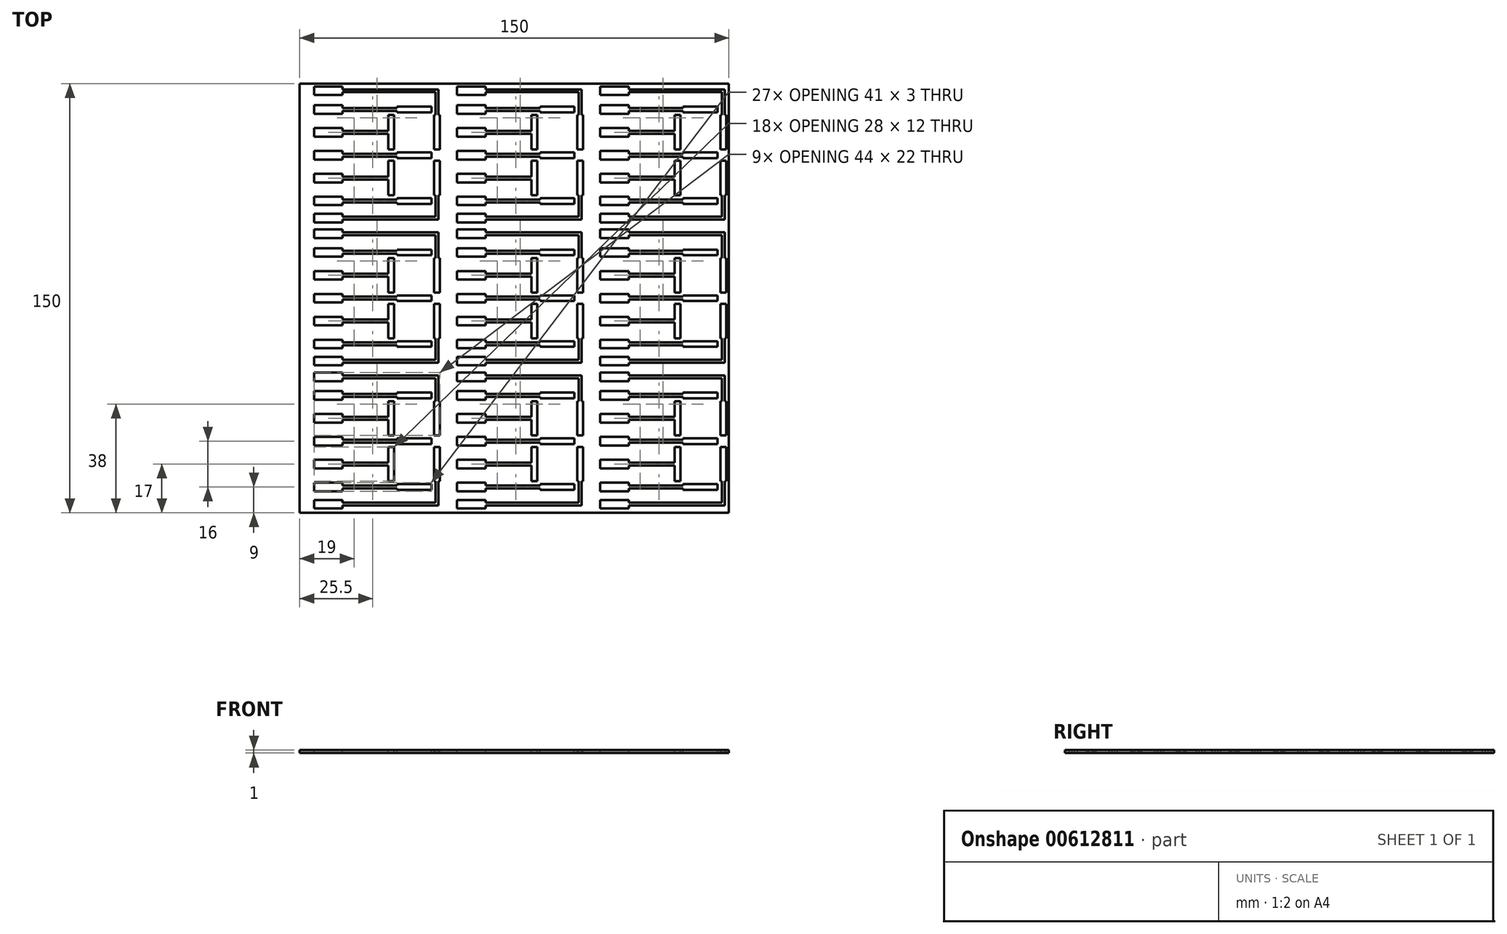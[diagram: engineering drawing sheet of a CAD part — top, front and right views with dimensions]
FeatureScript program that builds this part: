
annotation { "Feature Type Name" : "Feature", "Feature Type Description" : "" }
export const myFeature = defineFeature(function(context is Context, id is Id, definition is map)
    precondition{}
    {
        {
            var Q0;
            Q0=qCreatedBy(makeId("Top.planeOp"),FACE);
            var sketch = newSketch(context, id + "F0", { "sketchPlane" : qUnion([Q0])});
            skLineSegment(sketch, "E0.bottom", {"start": v(0, 0) * mm, "end": v(150, 0) * mm});
            skLineSegment(sketch, "E0.top", {"start": v(0, 150) * mm, "end": v(150, 150) * mm});
            skLineSegment(sketch, "E0.left", {"start": v(0, 0) * mm, "end": v(0, 150) * mm});
            skLineSegment(sketch, "E0.right", {"start": v(150, 0) * mm, "end": v(150, 150) * mm});
            skSolve(sketch);
        }
        {
            var Q0;
            Q0 = qSketchRegion(id + "F0", true);
            extrude(context, id + "F1", {"entities" : qUnion([Q0]), "depth" : 1 * mm, "offsetDistance" : 25 * mm});
        }
        {
            var Q0;
            Q0=makeQuery(id+"F1.opExtrude","CAP_FACE",FACE,{"disambiguationData":[OSD([sQuery(id+"F0.wireOp",EDGE,"E0.bottom"),sQuery(id+"F0.wireOp",EDGE,"E0.top"),sQuery(id+"F0.wireOp",EDGE,"E0.left"),sQuery(id+"F0.wireOp",EDGE,"E0.right")])],"isStart":false});
            var sketch = newSketch(context, id + "F2", { "sketchPlane" : qUnion([Q0])});
            skLineSegment(sketch, "E1", {"start": v(50, 150) * mm, "end": v(50, 0) * mm, "construction": true});
            skLineSegment(sketch, "E2", {"start": v(100, 150) * mm, "end": v(100, 0) * mm, "construction": true});
            skLineSegment(sketch, "E3", {"start": v(0, 100) * mm, "end": v(150, 100) * mm, "construction": true});
            skLineSegment(sketch, "E4", {"start": v(0, 50) * mm, "end": v(150, 50) * mm, "construction": true});
            skSolve(sketch);
        }
        {
            var Q0;
            Q0=makeQuery(id+"F2.imprint","IMPRINT",FACE,{"disambiguationData":[TD([[makeQuery(id+"F2.imprint","IMPRINT",EDGE,{"derivedFrom":makeQuery(id+"F1.opExtrude","CAP_EDGE",EDGE,{"disambiguationData":[OSD([sQuery(id+"F0.wireOp",EDGE,"E0.bottom")])],"isStart":false})}),1.0]])]});
            var sketch = newSketch(context, id + "F3", { "sketchPlane" : qUnion([Q0])});
            skLineSegment(sketch, "E5.bottom", {"start": v(34, 142) * mm, "end": v(46, 142) * mm});
            skLineSegment(sketch, "E5.top", {"start": v(34, 140) * mm, "end": v(46, 140) * mm});
            skLineSegment(sketch, "E5.left", {"start": v(34, 142) * mm, "end": v(34, 141.5) * mm});
            skLineSegment(sketch, "E5.right", {"start": v(46, 142) * mm, "end": v(46, 140) * mm});
            skLineSegment(sketch, "E6.bottom", {"start": v(47, 139) * mm, "end": v(49, 139) * mm});
            skLineSegment(sketch, "E6.top", {"start": v(47, 127) * mm, "end": v(49, 127) * mm});
            skLineSegment(sketch, "E6.left", {"start": v(47, 139) * mm, "end": v(47, 127) * mm});
            skLineSegment(sketch, "E6.right", {"start": v(49, 139) * mm, "end": v(49, 127) * mm});
            skLineSegment(sketch, "E7.bottom", {"start": v(46, 126) * mm, "end": v(34, 126) * mm});
            skLineSegment(sketch, "E7.top", {"start": v(46, 124) * mm, "end": v(34, 124) * mm});
            skLineSegment(sketch, "E7.left", {"start": v(46, 126) * mm, "end": v(46, 124) * mm});
            skLineSegment(sketch, "E7.right", {"start": v(34, 126) * mm, "end": v(34, 125.5) * mm});
            skLineSegment(sketch, "E8.bottom", {"start": v(47, 123) * mm, "end": v(49, 123) * mm});
            skLineSegment(sketch, "E8.top", {"start": v(47, 111) * mm, "end": v(47.5, 111) * mm});
            skLineSegment(sketch, "E8.left", {"start": v(47, 123) * mm, "end": v(47, 111) * mm});
            skLineSegment(sketch, "E8.right", {"start": v(49, 123) * mm, "end": v(49, 111) * mm});
            skLineSegment(sketch, "E9.bottom", {"start": v(46, 110) * mm, "end": v(34, 110) * mm});
            skLineSegment(sketch, "E9.top", {"start": v(46, 108) * mm, "end": v(34, 108) * mm});
            skLineSegment(sketch, "E9.left", {"start": v(46, 110) * mm, "end": v(46, 108) * mm});
            skLineSegment(sketch, "E9.right", {"start": v(34, 110) * mm, "end": v(34, 109.5) * mm});
            skLineSegment(sketch, "E10.bottom", {"start": v(33, 111) * mm, "end": v(31, 111) * mm});
            skLineSegment(sketch, "E10.top", {"start": v(33, 123) * mm, "end": v(31, 123) * mm});
            skLineSegment(sketch, "E10.left", {"start": v(33, 111) * mm, "end": v(33, 123) * mm});
            skLineSegment(sketch, "E10.right", {"start": v(31, 111) * mm, "end": v(31, 116.5) * mm});
            skLineSegment(sketch, "E11.bottom", {"start": v(33, 127) * mm, "end": v(31, 127) * mm});
            skLineSegment(sketch, "E11.top", {"start": v(33, 139) * mm, "end": v(31, 139) * mm});
            skLineSegment(sketch, "E11.left", {"start": v(33, 127) * mm, "end": v(33, 139) * mm});
            skLineSegment(sketch, "E11.right", {"start": v(31, 127) * mm, "end": v(31, 132.5) * mm});
            skLineSegment(sketch, "E12", {"start": v(48.5, 139) * mm, "end": v(48.5, 148) * mm});
            skLineSegment(sketch, "E13", {"start": v(48.5, 148) * mm, "end": v(15, 148) * mm});
            skLineSegment(sketch, "E14", {"start": v(47.5, 139) * mm, "end": v(47.5, 147) * mm});
            skLineSegment(sketch, "E15", {"start": v(47.5, 147) * mm, "end": v(15, 147) * mm});
            skLineSegment(sketch, "E16", {"start": v(15, 147) * mm, "end": v(15, 146) * mm});
            skLineSegment(sketch, "E17", {"start": v(15, 146) * mm, "end": v(5, 146) * mm});
            skLineSegment(sketch, "E18", {"start": v(5, 146) * mm, "end": v(5, 149) * mm});
            skLineSegment(sketch, "E19", {"start": v(5, 149) * mm, "end": v(15, 149) * mm});
            skLineSegment(sketch, "E20", {"start": v(15, 149) * mm, "end": v(15, 148) * mm});
            skLineSegment(sketch, "E21", {"start": v(34, 141.5) * mm, "end": v(15, 141.5) * mm});
            skLineSegment(sketch, "E22", {"start": v(34, 140.5) * mm, "end": v(15, 140.5) * mm});
            skLineSegment(sketch, "E23", {"start": v(15, 141.5) * mm, "end": v(15, 142.5) * mm});
            skLineSegment(sketch, "E24", {"start": v(15, 142.5) * mm, "end": v(5, 142.5) * mm});
            skLineSegment(sketch, "E25", {"start": v(5, 142.5) * mm, "end": v(5, 139.5) * mm});
            skLineSegment(sketch, "E26", {"start": v(5, 139.5) * mm, "end": v(15, 139.5) * mm});
            skLineSegment(sketch, "E27", {"start": v(15, 139.5) * mm, "end": v(15, 140.5) * mm});
            skLineSegment(sketch, "E28.trimOffspring", {"start": v(34, 140.5) * mm, "end": v(34, 140) * mm});
            skLineSegment(sketch, "E29.bottom", {"start": v(31, 133.5) * mm, "end": v(15, 133.5) * mm});
            skLineSegment(sketch, "E29.top", {"start": v(31, 132.5) * mm, "end": v(15, 132.5) * mm});
            skLineSegment(sketch, "E30.bottom", {"start": v(15, 134.5) * mm, "end": v(5, 134.5) * mm});
            skLineSegment(sketch, "E30.top", {"start": v(15, 131.5) * mm, "end": v(5, 131.5) * mm});
            skLineSegment(sketch, "E30.left", {"start": v(15, 134.5) * mm, "end": v(15, 133.5) * mm});
            skLineSegment(sketch, "E30.right", {"start": v(5, 134.5) * mm, "end": v(5, 131.5) * mm});
            skLineSegment(sketch, "E31.trimOffspring", {"start": v(15, 132.5) * mm, "end": v(15, 131.5) * mm});
            skLineSegment(sketch, "E32.trimOffspring", {"start": v(31, 133.5) * mm, "end": v(31, 139) * mm});
            skLineSegment(sketch, "E33.bottom", {"start": v(34, 125.5) * mm, "end": v(15, 125.5) * mm});
            skLineSegment(sketch, "E33.top", {"start": v(34, 124.5) * mm, "end": v(15, 124.5) * mm});
            skLineSegment(sketch, "E34.bottom", {"start": v(15, 126.5) * mm, "end": v(5, 126.5) * mm});
            skLineSegment(sketch, "E34.top", {"start": v(15, 123.5) * mm, "end": v(5, 123.5) * mm});
            skLineSegment(sketch, "E34.left", {"start": v(15, 126.5) * mm, "end": v(15, 125.5) * mm});
            skLineSegment(sketch, "E34.right", {"start": v(5, 126.5) * mm, "end": v(5, 123.5) * mm});
            skLineSegment(sketch, "E35.trimOffspring", {"start": v(15, 124.5) * mm, "end": v(15, 123.5) * mm});
            skLineSegment(sketch, "E36.bottom", {"start": v(31, 117.5) * mm, "end": v(15, 117.5) * mm});
            skLineSegment(sketch, "E36.top", {"start": v(31, 116.5) * mm, "end": v(15, 116.5) * mm});
            skLineSegment(sketch, "E37.bottom", {"start": v(15, 118.5) * mm, "end": v(5, 118.5) * mm});
            skLineSegment(sketch, "E37.top", {"start": v(15, 115.5) * mm, "end": v(5, 115.5) * mm});
            skLineSegment(sketch, "E37.left", {"start": v(15, 118.5) * mm, "end": v(15, 117.5) * mm});
            skLineSegment(sketch, "E37.right", {"start": v(5, 118.5) * mm, "end": v(5, 115.5) * mm});
            skLineSegment(sketch, "E38.trimOffspring", {"start": v(15, 116.5) * mm, "end": v(15, 115.5) * mm});
            skLineSegment(sketch, "E39.trimOffspring", {"start": v(31, 117.5) * mm, "end": v(31, 123) * mm});
            skLineSegment(sketch, "E40.trimOffspring", {"start": v(34, 124.5) * mm, "end": v(34, 124) * mm});
            skLineSegment(sketch, "E41.bottom", {"start": v(34, 109.5) * mm, "end": v(15, 109.5) * mm});
            skLineSegment(sketch, "E41.top", {"start": v(34, 108.5) * mm, "end": v(15, 108.5) * mm});
            skLineSegment(sketch, "E42.bottom", {"start": v(15, 110.5) * mm, "end": v(5, 110.5) * mm});
            skLineSegment(sketch, "E42.top", {"start": v(15, 107.5) * mm, "end": v(5, 107.5) * mm});
            skLineSegment(sketch, "E42.left", {"start": v(15, 110.5) * mm, "end": v(15, 109.5) * mm});
            skLineSegment(sketch, "E42.right", {"start": v(5, 110.5) * mm, "end": v(5, 107.5) * mm});
            skLineSegment(sketch, "E43.trimOffspring", {"start": v(15, 108.5) * mm, "end": v(15, 107.5) * mm});
            skLineSegment(sketch, "E44.trimOffspring", {"start": v(34, 108.5) * mm, "end": v(34, 108) * mm});
            skLineSegment(sketch, "E45.bottom", {"start": v(47.5, 103.5) * mm, "end": v(15, 103.5) * mm});
            skLineSegment(sketch, "E45.top", {"start": v(48.5, 102.5) * mm, "end": v(15, 102.5) * mm});
            skLineSegment(sketch, "E46.bottom", {"start": v(15, 104.5) * mm, "end": v(5, 104.5) * mm});
            skLineSegment(sketch, "E46.top", {"start": v(15, 101.5) * mm, "end": v(5, 101.5) * mm});
            skLineSegment(sketch, "E46.left", {"start": v(15, 104.5) * mm, "end": v(15, 103.5) * mm});
            skLineSegment(sketch, "E46.right", {"start": v(5, 104.5) * mm, "end": v(5, 101.5) * mm});
            skLineSegment(sketch, "E47.trimOffspring", {"start": v(15, 102.5) * mm, "end": v(15, 101.5) * mm});
            skLineSegment(sketch, "E48", {"start": v(48.5, 102.5) * mm, "end": v(48.5, 111) * mm});
            skLineSegment(sketch, "E49", {"start": v(47.5, 103.5) * mm, "end": v(47.5, 111) * mm});
            skLineSegment(sketch, "E50.trimOffspring", {"start": v(48.5, 111) * mm, "end": v(49, 111) * mm});
            skLineSegment(sketch, "E51.1.0.0", {"start": v(81, 127) * mm, "end": v(81, 132.5) * mm});
            skLineSegment(sketch, "E51.1.0.1", {"start": v(65, 118.5) * mm, "end": v(55, 118.5) * mm});
            skLineSegment(sketch, "E51.1.0.2", {"start": v(98.5, 102.5) * mm, "end": v(98.5, 111) * mm});
            skLineSegment(sketch, "E51.1.0.3", {"start": v(84, 109.5) * mm, "end": v(65, 109.5) * mm});
            skLineSegment(sketch, "E51.1.0.4", {"start": v(55, 139.5) * mm, "end": v(65, 139.5) * mm});
            skLineSegment(sketch, "E51.1.0.5", {"start": v(97.5, 147) * mm, "end": v(65, 147) * mm});
            skLineSegment(sketch, "E51.1.0.6", {"start": v(96, 110) * mm, "end": v(84, 110) * mm});
            skLineSegment(sketch, "E51.1.0.7", {"start": v(55, 110.5) * mm, "end": v(55, 107.5) * mm});
            skLineSegment(sketch, "E51.1.0.8", {"start": v(65, 146) * mm, "end": v(55, 146) * mm});
            skLineSegment(sketch, "E51.1.0.9", {"start": v(81, 116.5) * mm, "end": v(65, 116.5) * mm});
            skLineSegment(sketch, "E51.1.0.10", {"start": v(84, 124.5) * mm, "end": v(65, 124.5) * mm});
            skLineSegment(sketch, "E51.1.0.11", {"start": v(81, 117.5) * mm, "end": v(65, 117.5) * mm});
            skLineSegment(sketch, "E51.1.0.12", {"start": v(65, 131.5) * mm, "end": v(55, 131.5) * mm});
            skLineSegment(sketch, "E51.1.0.13", {"start": v(55, 118.5) * mm, "end": v(55, 115.5) * mm});
            skLineSegment(sketch, "E51.1.0.14", {"start": v(83, 111) * mm, "end": v(83, 123) * mm});
            skLineSegment(sketch, "E51.1.0.15", {"start": v(81, 111) * mm, "end": v(81, 116.5) * mm});
            skLineSegment(sketch, "E51.1.0.16", {"start": v(96, 108) * mm, "end": v(84, 108) * mm});
            skLineSegment(sketch, "E51.1.0.17", {"start": v(98.5, 148) * mm, "end": v(65, 148) * mm});
            skLineSegment(sketch, "E51.1.0.18", {"start": v(65, 104.5) * mm, "end": v(55, 104.5) * mm});
            skLineSegment(sketch, "E51.1.0.19", {"start": v(65, 134.5) * mm, "end": v(55, 134.5) * mm});
            skLineSegment(sketch, "E51.1.0.20", {"start": v(55, 126.5) * mm, "end": v(55, 123.5) * mm});
            skLineSegment(sketch, "E51.1.0.21", {"start": v(65, 107.5) * mm, "end": v(55, 107.5) * mm});
            skLineSegment(sketch, "E51.1.0.22", {"start": v(65, 110.5) * mm, "end": v(55, 110.5) * mm});
            skLineSegment(sketch, "E51.1.0.23", {"start": v(81, 133.5) * mm, "end": v(65, 133.5) * mm});
            skLineSegment(sketch, "E51.1.0.24", {"start": v(84, 140) * mm, "end": v(96, 140) * mm});
            skLineSegment(sketch, "E51.1.0.25", {"start": v(97.5, 103.5) * mm, "end": v(97.5, 111) * mm});
            skLineSegment(sketch, "E51.1.0.26", {"start": v(99, 123) * mm, "end": v(99, 111) * mm});
            skLineSegment(sketch, "E51.1.0.27", {"start": v(84, 141.5) * mm, "end": v(65, 141.5) * mm});
            skLineSegment(sketch, "E51.1.0.28", {"start": v(84, 108.5) * mm, "end": v(65, 108.5) * mm});
            skLineSegment(sketch, "E51.1.0.29", {"start": v(65, 123.5) * mm, "end": v(55, 123.5) * mm});
            skLineSegment(sketch, "E51.1.0.30", {"start": v(98.5, 139) * mm, "end": v(98.5, 148) * mm});
            skLineSegment(sketch, "E51.1.0.31", {"start": v(84, 125.5) * mm, "end": v(65, 125.5) * mm});
            skLineSegment(sketch, "E51.1.0.32", {"start": v(84, 140.5) * mm, "end": v(65, 140.5) * mm});
            skLineSegment(sketch, "E51.1.0.33", {"start": v(97, 123) * mm, "end": v(97, 111) * mm});
            skLineSegment(sketch, "E51.1.0.34", {"start": v(55, 142.5) * mm, "end": v(55, 139.5) * mm});
            skLineSegment(sketch, "E51.1.0.35", {"start": v(84, 142) * mm, "end": v(96, 142) * mm});
            skLineSegment(sketch, "E51.1.0.36", {"start": v(65, 126.5) * mm, "end": v(55, 126.5) * mm});
            skLineSegment(sketch, "E51.1.0.37", {"start": v(83, 127) * mm, "end": v(83, 139) * mm});
            skLineSegment(sketch, "E51.1.0.38", {"start": v(97.5, 103.5) * mm, "end": v(65, 103.5) * mm});
            skLineSegment(sketch, "E51.1.0.39", {"start": v(97, 139) * mm, "end": v(97, 127) * mm});
            skLineSegment(sketch, "E51.1.0.40", {"start": v(97.5, 139) * mm, "end": v(97.5, 147) * mm});
            skLineSegment(sketch, "E51.1.0.41", {"start": v(81, 132.5) * mm, "end": v(65, 132.5) * mm});
            skLineSegment(sketch, "E51.1.0.42", {"start": v(98.5, 102.5) * mm, "end": v(65, 102.5) * mm});
            skLineSegment(sketch, "E51.1.0.43", {"start": v(65, 115.5) * mm, "end": v(55, 115.5) * mm});
            skLineSegment(sketch, "E51.1.0.44", {"start": v(99, 139) * mm, "end": v(99, 127) * mm});
            skLineSegment(sketch, "E51.1.0.45", {"start": v(65, 101.5) * mm, "end": v(55, 101.5) * mm});
            skLineSegment(sketch, "E51.1.0.46", {"start": v(96, 126) * mm, "end": v(84, 126) * mm});
            skLineSegment(sketch, "E51.1.0.47", {"start": v(96, 124) * mm, "end": v(84, 124) * mm});
            skLineSegment(sketch, "E51.1.0.48", {"start": v(55, 134.5) * mm, "end": v(55, 131.5) * mm});
            skLineSegment(sketch, "E51.1.0.49", {"start": v(55, 104.5) * mm, "end": v(55, 101.5) * mm});
            skLineSegment(sketch, "E51.1.0.50", {"start": v(55, 146) * mm, "end": v(55, 149) * mm});
            skLineSegment(sketch, "E51.1.0.51", {"start": v(55, 149) * mm, "end": v(65, 149) * mm});
            skLineSegment(sketch, "E51.1.0.52", {"start": v(81, 117.5) * mm, "end": v(81, 123) * mm});
            skLineSegment(sketch, "E51.1.0.53", {"start": v(65, 142.5) * mm, "end": v(55, 142.5) * mm});
            skLineSegment(sketch, "E51.1.0.54", {"start": v(81, 133.5) * mm, "end": v(81, 139) * mm});
            skLineSegment(sketch, "E51.1.0.55", {"start": v(65, 118.5) * mm, "end": v(65, 117.5) * mm});
            skLineSegment(sketch, "E51.1.0.56", {"start": v(83, 123) * mm, "end": v(81, 123) * mm});
            skLineSegment(sketch, "E51.1.0.57", {"start": v(97, 111) * mm, "end": v(97.5, 111) * mm});
            skLineSegment(sketch, "E51.1.0.58", {"start": v(97, 127) * mm, "end": v(99, 127) * mm});
            skLineSegment(sketch, "E51.1.0.59", {"start": v(65, 126.5) * mm, "end": v(65, 125.5) * mm});
            skLineSegment(sketch, "E51.1.0.60", {"start": v(65, 141.5) * mm, "end": v(65, 142.5) * mm});
            skLineSegment(sketch, "E51.1.0.61", {"start": v(96, 126) * mm, "end": v(96, 124) * mm});
            skLineSegment(sketch, "E51.1.0.62", {"start": v(65, 134.5) * mm, "end": v(65, 133.5) * mm});
            skLineSegment(sketch, "E51.1.0.63", {"start": v(84, 110) * mm, "end": v(84, 109.5) * mm});
            skLineSegment(sketch, "E51.1.0.64", {"start": v(96, 142) * mm, "end": v(96, 140) * mm});
            skLineSegment(sketch, "E51.1.0.65", {"start": v(83, 111) * mm, "end": v(81, 111) * mm});
            skLineSegment(sketch, "E51.1.0.66", {"start": v(65, 110.5) * mm, "end": v(65, 109.5) * mm});
            skLineSegment(sketch, "E51.1.0.67", {"start": v(83, 127) * mm, "end": v(81, 127) * mm});
            skLineSegment(sketch, "E51.1.0.68", {"start": v(65, 102.5) * mm, "end": v(65, 101.5) * mm});
            skLineSegment(sketch, "E51.1.0.69", {"start": v(83, 139) * mm, "end": v(81, 139) * mm});
            skLineSegment(sketch, "E51.1.0.70", {"start": v(84, 142) * mm, "end": v(84, 141.5) * mm});
            skLineSegment(sketch, "E51.1.0.71", {"start": v(65, 104.5) * mm, "end": v(65, 103.5) * mm});
            skLineSegment(sketch, "E51.1.0.72", {"start": v(97, 123) * mm, "end": v(99, 123) * mm});
            skLineSegment(sketch, "E51.1.0.73", {"start": v(65, 116.5) * mm, "end": v(65, 115.5) * mm});
            skLineSegment(sketch, "E51.1.0.74", {"start": v(96, 110) * mm, "end": v(96, 108) * mm});
            skLineSegment(sketch, "E51.1.0.75", {"start": v(65, 108.5) * mm, "end": v(65, 107.5) * mm});
            skLineSegment(sketch, "E51.1.0.76", {"start": v(84, 126) * mm, "end": v(84, 125.5) * mm});
            skLineSegment(sketch, "E51.1.0.77", {"start": v(65, 124.5) * mm, "end": v(65, 123.5) * mm});
            skLineSegment(sketch, "E51.1.0.78", {"start": v(65, 139.5) * mm, "end": v(65, 140.5) * mm});
            skLineSegment(sketch, "E51.1.0.79", {"start": v(65, 149) * mm, "end": v(65, 148) * mm});
            skLineSegment(sketch, "E51.1.0.80", {"start": v(97, 139) * mm, "end": v(99, 139) * mm});
            skLineSegment(sketch, "E51.1.0.81", {"start": v(84, 124.5) * mm, "end": v(84, 124) * mm});
            skLineSegment(sketch, "E51.1.0.82", {"start": v(84, 108.5) * mm, "end": v(84, 108) * mm});
            skLineSegment(sketch, "E51.1.0.83", {"start": v(65, 132.5) * mm, "end": v(65, 131.5) * mm});
            skLineSegment(sketch, "E51.1.0.84", {"start": v(65, 147) * mm, "end": v(65, 146) * mm});
            skLineSegment(sketch, "E51.1.0.85", {"start": v(84, 140.5) * mm, "end": v(84, 140) * mm});
            skLineSegment(sketch, "E51.1.0.86", {"start": v(98.5, 111) * mm, "end": v(99, 111) * mm});
            skLineSegment(sketch, "E51.2.0.0", {"start": v(131, 127) * mm, "end": v(131, 132.5) * mm});
            skLineSegment(sketch, "E51.2.0.1", {"start": v(115, 118.5) * mm, "end": v(105, 118.5) * mm});
            skLineSegment(sketch, "E51.2.0.2", {"start": v(148.5, 102.5) * mm, "end": v(148.5, 111) * mm});
            skLineSegment(sketch, "E51.2.0.3", {"start": v(134, 109.5) * mm, "end": v(115, 109.5) * mm});
            skLineSegment(sketch, "E51.2.0.4", {"start": v(105, 139.5) * mm, "end": v(115, 139.5) * mm});
            skLineSegment(sketch, "E51.2.0.5", {"start": v(147.5, 147) * mm, "end": v(115, 147) * mm});
            skLineSegment(sketch, "E51.2.0.6", {"start": v(146, 110) * mm, "end": v(134, 110) * mm});
            skLineSegment(sketch, "E51.2.0.7", {"start": v(105, 110.5) * mm, "end": v(105, 107.5) * mm});
            skLineSegment(sketch, "E51.2.0.8", {"start": v(115, 146) * mm, "end": v(105, 146) * mm});
            skLineSegment(sketch, "E51.2.0.9", {"start": v(131, 116.5) * mm, "end": v(115, 116.5) * mm});
            skLineSegment(sketch, "E51.2.0.10", {"start": v(134, 124.5) * mm, "end": v(115, 124.5) * mm});
            skLineSegment(sketch, "E51.2.0.11", {"start": v(131, 117.5) * mm, "end": v(115, 117.5) * mm});
            skLineSegment(sketch, "E51.2.0.12", {"start": v(115, 131.5) * mm, "end": v(105, 131.5) * mm});
            skLineSegment(sketch, "E51.2.0.13", {"start": v(105, 118.5) * mm, "end": v(105, 115.5) * mm});
            skLineSegment(sketch, "E51.2.0.14", {"start": v(133, 111) * mm, "end": v(133, 123) * mm});
            skLineSegment(sketch, "E51.2.0.15", {"start": v(131, 111) * mm, "end": v(131, 116.5) * mm});
            skLineSegment(sketch, "E51.2.0.16", {"start": v(146, 108) * mm, "end": v(134, 108) * mm});
            skLineSegment(sketch, "E51.2.0.17", {"start": v(148.5, 148) * mm, "end": v(115, 148) * mm});
            skLineSegment(sketch, "E51.2.0.18", {"start": v(115, 104.5) * mm, "end": v(105, 104.5) * mm});
            skLineSegment(sketch, "E51.2.0.19", {"start": v(115, 134.5) * mm, "end": v(105, 134.5) * mm});
            skLineSegment(sketch, "E51.2.0.20", {"start": v(105, 126.5) * mm, "end": v(105, 123.5) * mm});
            skLineSegment(sketch, "E51.2.0.21", {"start": v(115, 107.5) * mm, "end": v(105, 107.5) * mm});
            skLineSegment(sketch, "E51.2.0.22", {"start": v(115, 110.5) * mm, "end": v(105, 110.5) * mm});
            skLineSegment(sketch, "E51.2.0.23", {"start": v(131, 133.5) * mm, "end": v(115, 133.5) * mm});
            skLineSegment(sketch, "E51.2.0.24", {"start": v(134, 140) * mm, "end": v(146, 140) * mm});
            skLineSegment(sketch, "E51.2.0.25", {"start": v(147.5, 103.5) * mm, "end": v(147.5, 111) * mm});
            skLineSegment(sketch, "E51.2.0.26", {"start": v(149, 123) * mm, "end": v(149, 111) * mm});
            skLineSegment(sketch, "E51.2.0.27", {"start": v(134, 141.5) * mm, "end": v(115, 141.5) * mm});
            skLineSegment(sketch, "E51.2.0.28", {"start": v(134, 108.5) * mm, "end": v(115, 108.5) * mm});
            skLineSegment(sketch, "E51.2.0.29", {"start": v(115, 123.5) * mm, "end": v(105, 123.5) * mm});
            skLineSegment(sketch, "E51.2.0.30", {"start": v(148.5, 139) * mm, "end": v(148.5, 148) * mm});
            skLineSegment(sketch, "E51.2.0.31", {"start": v(134, 125.5) * mm, "end": v(115, 125.5) * mm});
            skLineSegment(sketch, "E51.2.0.32", {"start": v(134, 140.5) * mm, "end": v(115, 140.5) * mm});
            skLineSegment(sketch, "E51.2.0.33", {"start": v(147, 123) * mm, "end": v(147, 111) * mm});
            skLineSegment(sketch, "E51.2.0.34", {"start": v(105, 142.5) * mm, "end": v(105, 139.5) * mm});
            skLineSegment(sketch, "E51.2.0.35", {"start": v(134, 142) * mm, "end": v(146, 142) * mm});
            skLineSegment(sketch, "E51.2.0.36", {"start": v(115, 126.5) * mm, "end": v(105, 126.5) * mm});
            skLineSegment(sketch, "E51.2.0.37", {"start": v(133, 127) * mm, "end": v(133, 139) * mm});
            skLineSegment(sketch, "E51.2.0.38", {"start": v(147.5, 103.5) * mm, "end": v(115, 103.5) * mm});
            skLineSegment(sketch, "E51.2.0.39", {"start": v(147, 139) * mm, "end": v(147, 127) * mm});
            skLineSegment(sketch, "E51.2.0.40", {"start": v(147.5, 139) * mm, "end": v(147.5, 147) * mm});
            skLineSegment(sketch, "E51.2.0.41", {"start": v(131, 132.5) * mm, "end": v(115, 132.5) * mm});
            skLineSegment(sketch, "E51.2.0.42", {"start": v(148.5, 102.5) * mm, "end": v(115, 102.5) * mm});
            skLineSegment(sketch, "E51.2.0.43", {"start": v(115, 115.5) * mm, "end": v(105, 115.5) * mm});
            skLineSegment(sketch, "E51.2.0.44", {"start": v(149, 139) * mm, "end": v(149, 127) * mm});
            skLineSegment(sketch, "E51.2.0.45", {"start": v(115, 101.5) * mm, "end": v(105, 101.5) * mm});
            skLineSegment(sketch, "E51.2.0.46", {"start": v(146, 126) * mm, "end": v(134, 126) * mm});
            skLineSegment(sketch, "E51.2.0.47", {"start": v(146, 124) * mm, "end": v(134, 124) * mm});
            skLineSegment(sketch, "E51.2.0.48", {"start": v(105, 134.5) * mm, "end": v(105, 131.5) * mm});
            skLineSegment(sketch, "E51.2.0.49", {"start": v(105, 104.5) * mm, "end": v(105, 101.5) * mm});
            skLineSegment(sketch, "E51.2.0.50", {"start": v(105, 146) * mm, "end": v(105, 149) * mm});
            skLineSegment(sketch, "E51.2.0.51", {"start": v(105, 149) * mm, "end": v(115, 149) * mm});
            skLineSegment(sketch, "E51.2.0.52", {"start": v(131, 117.5) * mm, "end": v(131, 123) * mm});
            skLineSegment(sketch, "E51.2.0.53", {"start": v(115, 142.5) * mm, "end": v(105, 142.5) * mm});
            skLineSegment(sketch, "E51.2.0.54", {"start": v(131, 133.5) * mm, "end": v(131, 139) * mm});
            skLineSegment(sketch, "E51.2.0.55", {"start": v(115, 118.5) * mm, "end": v(115, 117.5) * mm});
            skLineSegment(sketch, "E51.2.0.56", {"start": v(133, 123) * mm, "end": v(131, 123) * mm});
            skLineSegment(sketch, "E51.2.0.57", {"start": v(147, 111) * mm, "end": v(147.5, 111) * mm});
            skLineSegment(sketch, "E51.2.0.58", {"start": v(147, 127) * mm, "end": v(149, 127) * mm});
            skLineSegment(sketch, "E51.2.0.59", {"start": v(115, 126.5) * mm, "end": v(115, 125.5) * mm});
            skLineSegment(sketch, "E51.2.0.60", {"start": v(115, 141.5) * mm, "end": v(115, 142.5) * mm});
            skLineSegment(sketch, "E51.2.0.61", {"start": v(146, 126) * mm, "end": v(146, 124) * mm});
            skLineSegment(sketch, "E51.2.0.62", {"start": v(115, 134.5) * mm, "end": v(115, 133.5) * mm});
            skLineSegment(sketch, "E51.2.0.63", {"start": v(134, 110) * mm, "end": v(134, 109.5) * mm});
            skLineSegment(sketch, "E51.2.0.64", {"start": v(146, 142) * mm, "end": v(146, 140) * mm});
            skLineSegment(sketch, "E51.2.0.65", {"start": v(133, 111) * mm, "end": v(131, 111) * mm});
            skLineSegment(sketch, "E51.2.0.66", {"start": v(115, 110.5) * mm, "end": v(115, 109.5) * mm});
            skLineSegment(sketch, "E51.2.0.67", {"start": v(133, 127) * mm, "end": v(131, 127) * mm});
            skLineSegment(sketch, "E51.2.0.68", {"start": v(115, 102.5) * mm, "end": v(115, 101.5) * mm});
            skLineSegment(sketch, "E51.2.0.69", {"start": v(133, 139) * mm, "end": v(131, 139) * mm});
            skLineSegment(sketch, "E51.2.0.70", {"start": v(134, 142) * mm, "end": v(134, 141.5) * mm});
            skLineSegment(sketch, "E51.2.0.71", {"start": v(115, 104.5) * mm, "end": v(115, 103.5) * mm});
            skLineSegment(sketch, "E51.2.0.72", {"start": v(147, 123) * mm, "end": v(149, 123) * mm});
            skLineSegment(sketch, "E51.2.0.73", {"start": v(115, 116.5) * mm, "end": v(115, 115.5) * mm});
            skLineSegment(sketch, "E51.2.0.74", {"start": v(146, 110) * mm, "end": v(146, 108) * mm});
            skLineSegment(sketch, "E51.2.0.75", {"start": v(115, 108.5) * mm, "end": v(115, 107.5) * mm});
            skLineSegment(sketch, "E51.2.0.76", {"start": v(134, 126) * mm, "end": v(134, 125.5) * mm});
            skLineSegment(sketch, "E51.2.0.77", {"start": v(115, 124.5) * mm, "end": v(115, 123.5) * mm});
            skLineSegment(sketch, "E51.2.0.78", {"start": v(115, 139.5) * mm, "end": v(115, 140.5) * mm});
            skLineSegment(sketch, "E51.2.0.79", {"start": v(115, 149) * mm, "end": v(115, 148) * mm});
            skLineSegment(sketch, "E51.2.0.80", {"start": v(147, 139) * mm, "end": v(149, 139) * mm});
            skLineSegment(sketch, "E51.2.0.81", {"start": v(134, 124.5) * mm, "end": v(134, 124) * mm});
            skLineSegment(sketch, "E51.2.0.82", {"start": v(134, 108.5) * mm, "end": v(134, 108) * mm});
            skLineSegment(sketch, "E51.2.0.83", {"start": v(115, 132.5) * mm, "end": v(115, 131.5) * mm});
            skLineSegment(sketch, "E51.2.0.84", {"start": v(115, 147) * mm, "end": v(115, 146) * mm});
            skLineSegment(sketch, "E51.2.0.85", {"start": v(134, 140.5) * mm, "end": v(134, 140) * mm});
            skLineSegment(sketch, "E51.2.0.86", {"start": v(148.5, 111) * mm, "end": v(149, 111) * mm});
            skLineSegment(sketch, "E51.direction1", {"start": v(5, 101.5) * mm, "end": v(55, 101.5) * mm, "construction": true});
            skLineSegment(sketch, "E52.1.0.0", {"start": v(96, 58) * mm, "end": v(84, 58) * mm});
            skLineSegment(sketch, "E52.1.0.1", {"start": v(5, 92.5) * mm, "end": v(5, 89.5) * mm});
            skLineSegment(sketch, "E52.1.0.2", {"start": v(15, 76.5) * mm, "end": v(5, 76.5) * mm});
            skLineSegment(sketch, "E52.1.0.3", {"start": v(15, 54.5) * mm, "end": v(5, 54.5) * mm});
            skLineSegment(sketch, "E52.1.0.4", {"start": v(5, 54.5) * mm, "end": v(5, 51.5) * mm});
            skLineSegment(sketch, "E52.1.0.5", {"start": v(99, 73) * mm, "end": v(99, 61) * mm});
            skLineSegment(sketch, "E52.1.0.6", {"start": v(134, 75.5) * mm, "end": v(115, 75.5) * mm});
            skLineSegment(sketch, "E52.1.0.7", {"start": v(5, 51.5) * mm, "end": v(55, 51.5) * mm, "construction": true});
            skLineSegment(sketch, "E52.1.0.8", {"start": v(99, 89) * mm, "end": v(99, 77) * mm});
            skLineSegment(sketch, "E52.1.0.9", {"start": v(84, 75.5) * mm, "end": v(65, 75.5) * mm});
            skLineSegment(sketch, "E52.1.0.10", {"start": v(105, 84.5) * mm, "end": v(105, 81.5) * mm});
            skLineSegment(sketch, "E52.1.0.11", {"start": v(115, 51.5) * mm, "end": v(105, 51.5) * mm});
            skLineSegment(sketch, "E52.1.0.12", {"start": v(81, 67.5) * mm, "end": v(65, 67.5) * mm});
            skLineSegment(sketch, "E52.1.0.13", {"start": v(84, 59.5) * mm, "end": v(65, 59.5) * mm});
            skLineSegment(sketch, "E52.1.0.14", {"start": v(5, 68.5) * mm, "end": v(5, 65.5) * mm});
            skLineSegment(sketch, "E52.1.0.15", {"start": v(134, 92) * mm, "end": v(146, 92) * mm});
            skLineSegment(sketch, "E52.1.0.16", {"start": v(146, 58) * mm, "end": v(134, 58) * mm});
            skLineSegment(sketch, "E52.1.0.17", {"start": v(147.5, 89) * mm, "end": v(147.5, 97) * mm});
            skLineSegment(sketch, "E52.1.0.18", {"start": v(98.5, 52.5) * mm, "end": v(65, 52.5) * mm});
            skLineSegment(sketch, "E52.1.0.19", {"start": v(105, 54.5) * mm, "end": v(105, 51.5) * mm});
            skLineSegment(sketch, "E52.1.0.20", {"start": v(65, 84.5) * mm, "end": v(55, 84.5) * mm});
            skLineSegment(sketch, "E52.1.0.21", {"start": v(84, 92) * mm, "end": v(96, 92) * mm});
            skLineSegment(sketch, "E52.1.0.22", {"start": v(15, 57.5) * mm, "end": v(5, 57.5) * mm});
            skLineSegment(sketch, "E52.1.0.23", {"start": v(65, 81.5) * mm, "end": v(55, 81.5) * mm});
            skLineSegment(sketch, "E52.1.0.24", {"start": v(15, 84.5) * mm, "end": v(5, 84.5) * mm});
            skLineSegment(sketch, "E52.1.0.25", {"start": v(98.5, 89) * mm, "end": v(98.5, 98) * mm});
            skLineSegment(sketch, "E52.1.0.26", {"start": v(147.5, 53.5) * mm, "end": v(147.5, 61) * mm});
            skLineSegment(sketch, "E52.1.0.27", {"start": v(65, 65.5) * mm, "end": v(55, 65.5) * mm});
            skLineSegment(sketch, "E52.1.0.28", {"start": v(34, 74.5) * mm, "end": v(15, 74.5) * mm});
            skLineSegment(sketch, "E52.1.0.29", {"start": v(115, 81.5) * mm, "end": v(105, 81.5) * mm});
            skLineSegment(sketch, "E52.1.0.30", {"start": v(148.5, 89) * mm, "end": v(148.5, 98) * mm});
            skLineSegment(sketch, "E52.1.0.31", {"start": v(34, 90) * mm, "end": v(46, 90) * mm});
            skLineSegment(sketch, "E52.1.0.32", {"start": v(115, 68.5) * mm, "end": v(105, 68.5) * mm});
            skLineSegment(sketch, "E52.1.0.33", {"start": v(84, 91.5) * mm, "end": v(65, 91.5) * mm});
            skLineSegment(sketch, "E52.1.0.34", {"start": v(81, 83.5) * mm, "end": v(81, 89) * mm});
            skLineSegment(sketch, "E52.1.0.35", {"start": v(97.5, 53.5) * mm, "end": v(97.5, 61) * mm});
            skLineSegment(sketch, "E52.1.0.36", {"start": v(146, 76) * mm, "end": v(134, 76) * mm});
            skLineSegment(sketch, "E52.1.0.37", {"start": v(49, 73) * mm, "end": v(49, 61) * mm});
            skLineSegment(sketch, "E52.1.0.38", {"start": v(131, 77) * mm, "end": v(131, 82.5) * mm});
            skLineSegment(sketch, "E52.1.0.39", {"start": v(134, 90) * mm, "end": v(146, 90) * mm});
            skLineSegment(sketch, "E52.1.0.40", {"start": v(55, 54.5) * mm, "end": v(55, 51.5) * mm});
            skLineSegment(sketch, "E52.1.0.41", {"start": v(148.5, 52.5) * mm, "end": v(148.5, 61) * mm});
            skLineSegment(sketch, "E52.1.0.42", {"start": v(97.5, 97) * mm, "end": v(65, 97) * mm});
            skLineSegment(sketch, "E52.1.0.43", {"start": v(46, 76) * mm, "end": v(34, 76) * mm});
            skLineSegment(sketch, "E52.1.0.44", {"start": v(105, 99) * mm, "end": v(115, 99) * mm});
            skLineSegment(sketch, "E52.1.0.45", {"start": v(5, 76.5) * mm, "end": v(5, 73.5) * mm});
            skLineSegment(sketch, "E52.1.0.46", {"start": v(133, 61) * mm, "end": v(133, 73) * mm});
            skLineSegment(sketch, "E52.1.0.47", {"start": v(31, 83.5) * mm, "end": v(15, 83.5) * mm});
            skLineSegment(sketch, "E52.1.0.48", {"start": v(96, 60) * mm, "end": v(84, 60) * mm});
            skLineSegment(sketch, "E52.1.0.49", {"start": v(48.5, 52.5) * mm, "end": v(15, 52.5) * mm});
            skLineSegment(sketch, "E52.1.0.50", {"start": v(105, 68.5) * mm, "end": v(105, 65.5) * mm});
            skLineSegment(sketch, "E52.1.0.51", {"start": v(31, 67.5) * mm, "end": v(15, 67.5) * mm});
            skLineSegment(sketch, "E52.1.0.52", {"start": v(84, 74.5) * mm, "end": v(65, 74.5) * mm});
            skLineSegment(sketch, "E52.1.0.53", {"start": v(96, 76) * mm, "end": v(84, 76) * mm});
            skLineSegment(sketch, "E52.1.0.54", {"start": v(81, 77) * mm, "end": v(81, 82.5) * mm});
            skLineSegment(sketch, "E52.1.0.55", {"start": v(83, 77) * mm, "end": v(83, 89) * mm});
            skLineSegment(sketch, "E52.1.0.56", {"start": v(55, 92.5) * mm, "end": v(55, 89.5) * mm});
            skLineSegment(sketch, "E52.1.0.57", {"start": v(115, 96) * mm, "end": v(105, 96) * mm});
            skLineSegment(sketch, "E52.1.0.58", {"start": v(15, 65.5) * mm, "end": v(5, 65.5) * mm});
            skLineSegment(sketch, "E52.1.0.59", {"start": v(65, 96) * mm, "end": v(55, 96) * mm});
            skLineSegment(sketch, "E52.1.0.60", {"start": v(147, 73) * mm, "end": v(147, 61) * mm});
            skLineSegment(sketch, "E52.1.0.61", {"start": v(65, 57.5) * mm, "end": v(55, 57.5) * mm});
            skLineSegment(sketch, "E52.1.0.62", {"start": v(47.5, 53.5) * mm, "end": v(15, 53.5) * mm});
            skLineSegment(sketch, "E52.1.0.63", {"start": v(146, 74) * mm, "end": v(134, 74) * mm});
            skLineSegment(sketch, "E52.1.0.64", {"start": v(134, 59.5) * mm, "end": v(115, 59.5) * mm});
            skLineSegment(sketch, "E52.1.0.65", {"start": v(133, 77) * mm, "end": v(133, 89) * mm});
            skLineSegment(sketch, "E52.1.0.66", {"start": v(98.5, 98) * mm, "end": v(65, 98) * mm});
            skLineSegment(sketch, "E52.1.0.67", {"start": v(31, 82.5) * mm, "end": v(15, 82.5) * mm});
            skLineSegment(sketch, "E52.1.0.68", {"start": v(49, 89) * mm, "end": v(49, 77) * mm});
            skLineSegment(sketch, "E52.1.0.69", {"start": v(131, 61) * mm, "end": v(131, 66.5) * mm});
            skLineSegment(sketch, "E52.1.0.70", {"start": v(31, 66.5) * mm, "end": v(15, 66.5) * mm});
            skLineSegment(sketch, "E52.1.0.71", {"start": v(5, 89.5) * mm, "end": v(15, 89.5) * mm});
            skLineSegment(sketch, "E52.1.0.72", {"start": v(55, 99) * mm, "end": v(65, 99) * mm});
            skLineSegment(sketch, "E52.1.0.73", {"start": v(81, 67.5) * mm, "end": v(81, 73) * mm});
            skLineSegment(sketch, "E52.1.0.74", {"start": v(65, 76.5) * mm, "end": v(55, 76.5) * mm});
            skLineSegment(sketch, "E52.1.0.75", {"start": v(115, 73.5) * mm, "end": v(105, 73.5) * mm});
            skLineSegment(sketch, "E52.1.0.76", {"start": v(115, 84.5) * mm, "end": v(105, 84.5) * mm});
            skLineSegment(sketch, "E52.1.0.77", {"start": v(5, 84.5) * mm, "end": v(5, 81.5) * mm});
            skLineSegment(sketch, "E52.1.0.78", {"start": v(115, 76.5) * mm, "end": v(105, 76.5) * mm});
            skLineSegment(sketch, "E52.1.0.79", {"start": v(47.5, 89) * mm, "end": v(47.5, 97) * mm});
            skLineSegment(sketch, "E52.1.0.80", {"start": v(148.5, 52.5) * mm, "end": v(115, 52.5) * mm});
            skLineSegment(sketch, "E52.1.0.81", {"start": v(134, 90.5) * mm, "end": v(115, 90.5) * mm});
            skLineSegment(sketch, "E52.1.0.82", {"start": v(105, 89.5) * mm, "end": v(115, 89.5) * mm});
            skLineSegment(sketch, "E52.1.0.83", {"start": v(65, 60.5) * mm, "end": v(55, 60.5) * mm});
            skLineSegment(sketch, "E52.1.0.84", {"start": v(33, 77) * mm, "end": v(33, 89) * mm});
            skLineSegment(sketch, "E52.1.0.85", {"start": v(97, 73) * mm, "end": v(97, 61) * mm});
            skLineSegment(sketch, "E52.1.0.86", {"start": v(147.5, 97) * mm, "end": v(115, 97) * mm});
            skLineSegment(sketch, "E52.1.0.87", {"start": v(105, 76.5) * mm, "end": v(105, 73.5) * mm});
            skLineSegment(sketch, "E52.1.0.88", {"start": v(97, 89) * mm, "end": v(97, 77) * mm});
            skLineSegment(sketch, "E52.1.0.89", {"start": v(34, 92) * mm, "end": v(46, 92) * mm});
            skLineSegment(sketch, "E52.1.0.90", {"start": v(149, 89) * mm, "end": v(149, 77) * mm});
            skLineSegment(sketch, "E52.1.0.91", {"start": v(147, 89) * mm, "end": v(147, 77) * mm});
            skLineSegment(sketch, "E52.1.0.92", {"start": v(34, 90.5) * mm, "end": v(15, 90.5) * mm});
            skLineSegment(sketch, "E52.1.0.93", {"start": v(97.5, 53.5) * mm, "end": v(65, 53.5) * mm});
            skLineSegment(sketch, "E52.1.0.94", {"start": v(5, 60.5) * mm, "end": v(5, 57.5) * mm});
            skLineSegment(sketch, "E52.1.0.95", {"start": v(5, 99) * mm, "end": v(15, 99) * mm});
            skLineSegment(sketch, "E52.1.0.96", {"start": v(134, 74.5) * mm, "end": v(115, 74.5) * mm});
            skLineSegment(sketch, "E52.1.0.97", {"start": v(81, 83.5) * mm, "end": v(65, 83.5) * mm});
            skLineSegment(sketch, "E52.1.0.98", {"start": v(134, 58.5) * mm, "end": v(115, 58.5) * mm});
            skLineSegment(sketch, "E52.1.0.99", {"start": v(65, 68.5) * mm, "end": v(55, 68.5) * mm});
            skLineSegment(sketch, "E52.1.0.100", {"start": v(34, 58.5) * mm, "end": v(15, 58.5) * mm});
            skLineSegment(sketch, "E52.1.0.101", {"start": v(15, 96) * mm, "end": v(5, 96) * mm});
            skLineSegment(sketch, "E52.1.0.102", {"start": v(47, 89) * mm, "end": v(47, 77) * mm});
            skLineSegment(sketch, "E52.1.0.103", {"start": v(15, 73.5) * mm, "end": v(5, 73.5) * mm});
            skLineSegment(sketch, "E52.1.0.104", {"start": v(115, 57.5) * mm, "end": v(105, 57.5) * mm});
            skLineSegment(sketch, "E52.1.0.105", {"start": v(5, 96) * mm, "end": v(5, 99) * mm});
            skLineSegment(sketch, "E52.1.0.106", {"start": v(55, 60.5) * mm, "end": v(55, 57.5) * mm});
            skLineSegment(sketch, "E52.1.0.107", {"start": v(46, 74) * mm, "end": v(34, 74) * mm});
            skLineSegment(sketch, "E52.1.0.108", {"start": v(48.5, 98) * mm, "end": v(15, 98) * mm});
            skLineSegment(sketch, "E52.1.0.109", {"start": v(31, 67.5) * mm, "end": v(31, 73) * mm});
            skLineSegment(sketch, "E52.1.0.110", {"start": v(15, 68.5) * mm, "end": v(5, 68.5) * mm});
            skLineSegment(sketch, "E52.1.0.111", {"start": v(47, 73) * mm, "end": v(47, 61) * mm});
            skLineSegment(sketch, "E52.1.0.112", {"start": v(131, 67.5) * mm, "end": v(131, 73) * mm});
            skLineSegment(sketch, "E52.1.0.113", {"start": v(84, 58.5) * mm, "end": v(65, 58.5) * mm});
            skLineSegment(sketch, "E52.1.0.114", {"start": v(46, 58) * mm, "end": v(34, 58) * mm});
            skLineSegment(sketch, "E52.1.0.115", {"start": v(149, 73) * mm, "end": v(149, 61) * mm});
            skLineSegment(sketch, "E52.1.0.116", {"start": v(115, 92.5) * mm, "end": v(105, 92.5) * mm});
            skLineSegment(sketch, "E52.1.0.117", {"start": v(65, 54.5) * mm, "end": v(55, 54.5) * mm});
            skLineSegment(sketch, "E52.1.0.118", {"start": v(131, 83.5) * mm, "end": v(115, 83.5) * mm});
            skLineSegment(sketch, "E52.1.0.119", {"start": v(83, 61) * mm, "end": v(83, 73) * mm});
            skLineSegment(sketch, "E52.1.0.120", {"start": v(55, 89.5) * mm, "end": v(65, 89.5) * mm});
            skLineSegment(sketch, "E52.1.0.121", {"start": v(131, 66.5) * mm, "end": v(115, 66.5) * mm});
            skLineSegment(sketch, "E52.1.0.122", {"start": v(84, 90.5) * mm, "end": v(65, 90.5) * mm});
            skLineSegment(sketch, "E52.1.0.123", {"start": v(131, 67.5) * mm, "end": v(115, 67.5) * mm});
            skLineSegment(sketch, "E52.1.0.124", {"start": v(131, 82.5) * mm, "end": v(115, 82.5) * mm});
            skLineSegment(sketch, "E52.1.0.125", {"start": v(55, 84.5) * mm, "end": v(55, 81.5) * mm});
            skLineSegment(sketch, "E52.1.0.126", {"start": v(115, 65.5) * mm, "end": v(105, 65.5) * mm});
            skLineSegment(sketch, "E52.1.0.127", {"start": v(15, 60.5) * mm, "end": v(5, 60.5) * mm});
            skLineSegment(sketch, "E52.1.0.128", {"start": v(105, 92.5) * mm, "end": v(105, 89.5) * mm});
            skLineSegment(sketch, "E52.1.0.129", {"start": v(134, 91.5) * mm, "end": v(115, 91.5) * mm});
            skLineSegment(sketch, "E52.1.0.130", {"start": v(46, 60) * mm, "end": v(34, 60) * mm});
            skLineSegment(sketch, "E52.1.0.131", {"start": v(31, 61) * mm, "end": v(31, 66.5) * mm});
            skLineSegment(sketch, "E52.1.0.132", {"start": v(15, 81.5) * mm, "end": v(5, 81.5) * mm});
            skLineSegment(sketch, "E52.1.0.133", {"start": v(105, 96) * mm, "end": v(105, 99) * mm});
            skLineSegment(sketch, "E52.1.0.134", {"start": v(115, 54.5) * mm, "end": v(105, 54.5) * mm});
            skLineSegment(sketch, "E52.1.0.135", {"start": v(81, 66.5) * mm, "end": v(65, 66.5) * mm});
            skLineSegment(sketch, "E52.1.0.136", {"start": v(81, 82.5) * mm, "end": v(65, 82.5) * mm});
            skLineSegment(sketch, "E52.1.0.137", {"start": v(65, 92.5) * mm, "end": v(55, 92.5) * mm});
            skLineSegment(sketch, "E52.1.0.138", {"start": v(48.5, 89) * mm, "end": v(48.5, 98) * mm});
            skLineSegment(sketch, "E52.1.0.139", {"start": v(81, 61) * mm, "end": v(81, 66.5) * mm});
            skLineSegment(sketch, "E52.1.0.140", {"start": v(97.5, 89) * mm, "end": v(97.5, 97) * mm});
            skLineSegment(sketch, "E52.1.0.141", {"start": v(84, 90) * mm, "end": v(96, 90) * mm});
            skLineSegment(sketch, "E52.1.0.142", {"start": v(98.5, 52.5) * mm, "end": v(98.5, 61) * mm});
            skLineSegment(sketch, "E52.1.0.143", {"start": v(47.5, 97) * mm, "end": v(15, 97) * mm});
            skLineSegment(sketch, "E52.1.0.144", {"start": v(96, 74) * mm, "end": v(84, 74) * mm});
            skLineSegment(sketch, "E52.1.0.145", {"start": v(148.5, 98) * mm, "end": v(115, 98) * mm});
            skLineSegment(sketch, "E52.1.0.146", {"start": v(33, 61) * mm, "end": v(33, 73) * mm});
            skLineSegment(sketch, "E52.1.0.147", {"start": v(55, 96) * mm, "end": v(55, 99) * mm});
            skLineSegment(sketch, "E52.1.0.148", {"start": v(34, 59.5) * mm, "end": v(15, 59.5) * mm});
            skLineSegment(sketch, "E52.1.0.149", {"start": v(31, 77) * mm, "end": v(31, 82.5) * mm});
            skLineSegment(sketch, "E52.1.0.150", {"start": v(34, 91.5) * mm, "end": v(15, 91.5) * mm});
            skLineSegment(sketch, "E52.1.0.151", {"start": v(34, 75.5) * mm, "end": v(15, 75.5) * mm});
            skLineSegment(sketch, "E52.1.0.152", {"start": v(47.5, 53.5) * mm, "end": v(47.5, 61) * mm});
            skLineSegment(sketch, "E52.1.0.153", {"start": v(105, 60.5) * mm, "end": v(105, 57.5) * mm});
            skLineSegment(sketch, "E52.1.0.154", {"start": v(65, 51.5) * mm, "end": v(55, 51.5) * mm});
            skLineSegment(sketch, "E52.1.0.155", {"start": v(65, 73.5) * mm, "end": v(55, 73.5) * mm});
            skLineSegment(sketch, "E52.1.0.156", {"start": v(55, 68.5) * mm, "end": v(55, 65.5) * mm});
            skLineSegment(sketch, "E52.1.0.157", {"start": v(48.5, 52.5) * mm, "end": v(48.5, 61) * mm});
            skLineSegment(sketch, "E52.1.0.158", {"start": v(115, 60.5) * mm, "end": v(105, 60.5) * mm});
            skLineSegment(sketch, "E52.1.0.159", {"start": v(146, 60) * mm, "end": v(134, 60) * mm});
            skLineSegment(sketch, "E52.1.0.160", {"start": v(131, 83.5) * mm, "end": v(131, 89) * mm});
            skLineSegment(sketch, "E52.1.0.161", {"start": v(147.5, 53.5) * mm, "end": v(115, 53.5) * mm});
            skLineSegment(sketch, "E52.1.0.162", {"start": v(15, 92.5) * mm, "end": v(5, 92.5) * mm});
            skLineSegment(sketch, "E52.1.0.163", {"start": v(15, 51.5) * mm, "end": v(5, 51.5) * mm});
            skLineSegment(sketch, "E52.1.0.164", {"start": v(55, 76.5) * mm, "end": v(55, 73.5) * mm});
            skLineSegment(sketch, "E52.1.0.165", {"start": v(31, 83.5) * mm, "end": v(31, 89) * mm});
            skLineSegment(sketch, "E52.1.0.166", {"start": v(84, 92) * mm, "end": v(84, 91.5) * mm});
            skLineSegment(sketch, "E52.1.0.167", {"start": v(84, 58.5) * mm, "end": v(84, 58) * mm});
            skLineSegment(sketch, "E52.1.0.168", {"start": v(46, 76) * mm, "end": v(46, 74) * mm});
            skLineSegment(sketch, "E52.1.0.169", {"start": v(34, 92) * mm, "end": v(34, 91.5) * mm});
            skLineSegment(sketch, "E52.1.0.170", {"start": v(15, 54.5) * mm, "end": v(15, 53.5) * mm});
            skLineSegment(sketch, "E52.1.0.171", {"start": v(115, 97) * mm, "end": v(115, 96) * mm});
            skLineSegment(sketch, "E52.1.0.172", {"start": v(115, 84.5) * mm, "end": v(115, 83.5) * mm});
            skLineSegment(sketch, "E52.1.0.173", {"start": v(146, 60) * mm, "end": v(146, 58) * mm});
            skLineSegment(sketch, "E52.1.0.174", {"start": v(15, 68.5) * mm, "end": v(15, 67.5) * mm});
            skLineSegment(sketch, "E52.1.0.175", {"start": v(15, 84.5) * mm, "end": v(15, 83.5) * mm});
            skLineSegment(sketch, "E52.1.0.176", {"start": v(133, 77) * mm, "end": v(131, 77) * mm});
            skLineSegment(sketch, "E52.1.0.177", {"start": v(134, 58.5) * mm, "end": v(134, 58) * mm});
            skLineSegment(sketch, "E52.1.0.178", {"start": v(133, 61) * mm, "end": v(131, 61) * mm});
            skLineSegment(sketch, "E52.1.0.179", {"start": v(34, 60) * mm, "end": v(34, 59.5) * mm});
            skLineSegment(sketch, "E52.1.0.180", {"start": v(146, 76) * mm, "end": v(146, 74) * mm});
            skLineSegment(sketch, "E52.1.0.181", {"start": v(83, 89) * mm, "end": v(81, 89) * mm});
            skLineSegment(sketch, "E52.1.0.182", {"start": v(97, 89) * mm, "end": v(99, 89) * mm});
            skLineSegment(sketch, "E52.1.0.183", {"start": v(47, 77) * mm, "end": v(49, 77) * mm});
            skLineSegment(sketch, "E52.1.0.184", {"start": v(146, 92) * mm, "end": v(146, 90) * mm});
            skLineSegment(sketch, "E52.1.0.185", {"start": v(15, 66.5) * mm, "end": v(15, 65.5) * mm});
            skLineSegment(sketch, "E52.1.0.186", {"start": v(33, 77) * mm, "end": v(31, 77) * mm});
            skLineSegment(sketch, "E52.1.0.187", {"start": v(47, 73) * mm, "end": v(49, 73) * mm});
            skLineSegment(sketch, "E52.1.0.188", {"start": v(65, 97) * mm, "end": v(65, 96) * mm});
            skLineSegment(sketch, "E52.1.0.189", {"start": v(134, 60) * mm, "end": v(134, 59.5) * mm});
            skLineSegment(sketch, "E52.1.0.190", {"start": v(65, 54.5) * mm, "end": v(65, 53.5) * mm});
            skLineSegment(sketch, "E52.1.0.191", {"start": v(97, 77) * mm, "end": v(99, 77) * mm});
            skLineSegment(sketch, "E52.1.0.192", {"start": v(147, 89) * mm, "end": v(149, 89) * mm});
            skLineSegment(sketch, "E52.1.0.193", {"start": v(65, 68.5) * mm, "end": v(65, 67.5) * mm});
            skLineSegment(sketch, "E52.1.0.194", {"start": v(33, 89) * mm, "end": v(31, 89) * mm});
            skLineSegment(sketch, "E52.1.0.195", {"start": v(147, 77) * mm, "end": v(149, 77) * mm});
            skLineSegment(sketch, "E52.1.0.196", {"start": v(133, 89) * mm, "end": v(131, 89) * mm});
            skLineSegment(sketch, "E52.1.0.197", {"start": v(98.5, 61) * mm, "end": v(99, 61) * mm});
            skLineSegment(sketch, "E52.1.0.198", {"start": v(46, 60) * mm, "end": v(46, 58) * mm});
            skLineSegment(sketch, "E52.1.0.199", {"start": v(83, 77) * mm, "end": v(81, 77) * mm});
            skLineSegment(sketch, "E52.1.0.200", {"start": v(84, 74.5) * mm, "end": v(84, 74) * mm});
            skLineSegment(sketch, "E52.1.0.201", {"start": v(96, 60) * mm, "end": v(96, 58) * mm});
            skLineSegment(sketch, "E52.1.0.202", {"start": v(46, 92) * mm, "end": v(46, 90) * mm});
            skLineSegment(sketch, "E52.1.0.203", {"start": v(133, 73) * mm, "end": v(131, 73) * mm});
            skLineSegment(sketch, "E52.1.0.204", {"start": v(47, 61) * mm, "end": v(47.5, 61) * mm});
            skLineSegment(sketch, "E52.1.0.205", {"start": v(147, 73) * mm, "end": v(149, 73) * mm});
            skLineSegment(sketch, "E52.1.0.206", {"start": v(83, 61) * mm, "end": v(81, 61) * mm});
            skLineSegment(sketch, "E52.1.0.207", {"start": v(115, 54.5) * mm, "end": v(115, 53.5) * mm});
            skLineSegment(sketch, "E52.1.0.208", {"start": v(147, 61) * mm, "end": v(147.5, 61) * mm});
            skLineSegment(sketch, "E52.1.0.209", {"start": v(96, 92) * mm, "end": v(96, 90) * mm});
            skLineSegment(sketch, "E52.1.0.210", {"start": v(115, 76.5) * mm, "end": v(115, 75.5) * mm});
            skLineSegment(sketch, "E52.1.0.211", {"start": v(15, 91.5) * mm, "end": v(15, 92.5) * mm});
            skLineSegment(sketch, "E52.1.0.212", {"start": v(97, 61) * mm, "end": v(97.5, 61) * mm});
            skLineSegment(sketch, "E52.1.0.213", {"start": v(83, 73) * mm, "end": v(81, 73) * mm});
            skLineSegment(sketch, "E52.1.0.214", {"start": v(97, 73) * mm, "end": v(99, 73) * mm});
            skLineSegment(sketch, "E52.1.0.215", {"start": v(15, 60.5) * mm, "end": v(15, 59.5) * mm});
            skLineSegment(sketch, "E52.1.0.216", {"start": v(15, 76.5) * mm, "end": v(15, 75.5) * mm});
            skLineSegment(sketch, "E52.1.0.217", {"start": v(115, 68.5) * mm, "end": v(115, 67.5) * mm});
            skLineSegment(sketch, "E52.1.0.218", {"start": v(33, 73) * mm, "end": v(31, 73) * mm});
            skLineSegment(sketch, "E52.1.0.219", {"start": v(33, 61) * mm, "end": v(31, 61) * mm});
            skLineSegment(sketch, "E52.1.0.220", {"start": v(134, 76) * mm, "end": v(134, 75.5) * mm});
            skLineSegment(sketch, "E52.1.0.221", {"start": v(96, 76) * mm, "end": v(96, 74) * mm});
            skLineSegment(sketch, "E52.1.0.222", {"start": v(148.5, 61) * mm, "end": v(149, 61) * mm});
            skLineSegment(sketch, "E52.1.0.223", {"start": v(34, 58.5) * mm, "end": v(34, 58) * mm});
            skLineSegment(sketch, "E52.1.0.224", {"start": v(15, 58.5) * mm, "end": v(15, 57.5) * mm});
            skLineSegment(sketch, "E52.1.0.225", {"start": v(84, 76) * mm, "end": v(84, 75.5) * mm});
            skLineSegment(sketch, "E52.1.0.226", {"start": v(15, 82.5) * mm, "end": v(15, 81.5) * mm});
            skLineSegment(sketch, "E52.1.0.227", {"start": v(34, 76) * mm, "end": v(34, 75.5) * mm});
            skLineSegment(sketch, "E52.1.0.228", {"start": v(134, 74.5) * mm, "end": v(134, 74) * mm});
            skLineSegment(sketch, "E52.1.0.229", {"start": v(15, 52.5) * mm, "end": v(15, 51.5) * mm});
            skLineSegment(sketch, "E52.1.0.230", {"start": v(48.5, 61) * mm, "end": v(49, 61) * mm});
            skLineSegment(sketch, "E52.1.0.231", {"start": v(115, 91.5) * mm, "end": v(115, 92.5) * mm});
            skLineSegment(sketch, "E52.1.0.232", {"start": v(115, 89.5) * mm, "end": v(115, 90.5) * mm});
            skLineSegment(sketch, "E52.1.0.233", {"start": v(65, 82.5) * mm, "end": v(65, 81.5) * mm});
            skLineSegment(sketch, "E52.1.0.234", {"start": v(65, 58.5) * mm, "end": v(65, 57.5) * mm});
            skLineSegment(sketch, "E52.1.0.235", {"start": v(47, 89) * mm, "end": v(49, 89) * mm});
            skLineSegment(sketch, "E52.1.0.236", {"start": v(34, 74.5) * mm, "end": v(34, 74) * mm});
            skLineSegment(sketch, "E52.1.0.237", {"start": v(115, 99) * mm, "end": v(115, 98) * mm});
            skLineSegment(sketch, "E52.1.0.238", {"start": v(134, 90.5) * mm, "end": v(134, 90) * mm});
            skLineSegment(sketch, "E52.1.0.239", {"start": v(65, 91.5) * mm, "end": v(65, 92.5) * mm});
            skLineSegment(sketch, "E52.1.0.240", {"start": v(65, 76.5) * mm, "end": v(65, 75.5) * mm});
            skLineSegment(sketch, "E52.1.0.241", {"start": v(84, 60) * mm, "end": v(84, 59.5) * mm});
            skLineSegment(sketch, "E52.1.0.242", {"start": v(115, 74.5) * mm, "end": v(115, 73.5) * mm});
            skLineSegment(sketch, "E52.1.0.243", {"start": v(65, 52.5) * mm, "end": v(65, 51.5) * mm});
            skLineSegment(sketch, "E52.1.0.244", {"start": v(65, 99) * mm, "end": v(65, 98) * mm});
            skLineSegment(sketch, "E52.1.0.245", {"start": v(115, 58.5) * mm, "end": v(115, 57.5) * mm});
            skLineSegment(sketch, "E52.1.0.246", {"start": v(115, 60.5) * mm, "end": v(115, 59.5) * mm});
            skLineSegment(sketch, "E52.1.0.247", {"start": v(65, 66.5) * mm, "end": v(65, 65.5) * mm});
            skLineSegment(sketch, "E52.1.0.248", {"start": v(84, 90.5) * mm, "end": v(84, 90) * mm});
            skLineSegment(sketch, "E52.1.0.249", {"start": v(65, 60.5) * mm, "end": v(65, 59.5) * mm});
            skLineSegment(sketch, "E52.1.0.250", {"start": v(15, 89.5) * mm, "end": v(15, 90.5) * mm});
            skLineSegment(sketch, "E52.1.0.251", {"start": v(15, 74.5) * mm, "end": v(15, 73.5) * mm});
            skLineSegment(sketch, "E52.1.0.252", {"start": v(65, 89.5) * mm, "end": v(65, 90.5) * mm});
            skLineSegment(sketch, "E52.1.0.253", {"start": v(65, 84.5) * mm, "end": v(65, 83.5) * mm});
            skLineSegment(sketch, "E52.1.0.254", {"start": v(15, 99) * mm, "end": v(15, 98) * mm});
            skLineSegment(sketch, "E52.1.0.255", {"start": v(65, 74.5) * mm, "end": v(65, 73.5) * mm});
            skLineSegment(sketch, "E52.1.0.256", {"start": v(134, 92) * mm, "end": v(134, 91.5) * mm});
            skLineSegment(sketch, "E52.1.0.257", {"start": v(115, 52.5) * mm, "end": v(115, 51.5) * mm});
            skLineSegment(sketch, "E52.1.0.258", {"start": v(115, 66.5) * mm, "end": v(115, 65.5) * mm});
            skLineSegment(sketch, "E52.1.0.259", {"start": v(115, 82.5) * mm, "end": v(115, 81.5) * mm});
            skLineSegment(sketch, "E52.1.0.260", {"start": v(15, 97) * mm, "end": v(15, 96) * mm});
            skLineSegment(sketch, "E52.1.0.261", {"start": v(34, 90.5) * mm, "end": v(34, 90) * mm});
            skLineSegment(sketch, "E52.2.0.0", {"start": v(96, 8) * mm, "end": v(84, 8) * mm});
            skLineSegment(sketch, "E52.2.0.1", {"start": v(5, 42.5) * mm, "end": v(5, 39.5) * mm});
            skLineSegment(sketch, "E52.2.0.2", {"start": v(15, 26.5) * mm, "end": v(5, 26.5) * mm});
            skLineSegment(sketch, "E52.2.0.3", {"start": v(15, 4.5) * mm, "end": v(5, 4.5) * mm});
            skLineSegment(sketch, "E52.2.0.4", {"start": v(5, 4.5) * mm, "end": v(5, 1.5) * mm});
            skLineSegment(sketch, "E52.2.0.5", {"start": v(99, 23) * mm, "end": v(99, 11) * mm});
            skLineSegment(sketch, "E52.2.0.6", {"start": v(134, 25.5) * mm, "end": v(115, 25.5) * mm});
            skLineSegment(sketch, "E52.2.0.7", {"start": v(5, 1.5) * mm, "end": v(55, 1.5) * mm, "construction": true});
            skLineSegment(sketch, "E52.2.0.8", {"start": v(99, 39) * mm, "end": v(99, 27) * mm});
            skLineSegment(sketch, "E52.2.0.9", {"start": v(84, 25.5) * mm, "end": v(65, 25.5) * mm});
            skLineSegment(sketch, "E52.2.0.10", {"start": v(105, 34.5) * mm, "end": v(105, 31.5) * mm});
            skLineSegment(sketch, "E52.2.0.11", {"start": v(115, 1.5) * mm, "end": v(105, 1.5) * mm});
            skLineSegment(sketch, "E52.2.0.12", {"start": v(81, 17.5) * mm, "end": v(65, 17.5) * mm});
            skLineSegment(sketch, "E52.2.0.13", {"start": v(84, 9.5) * mm, "end": v(65, 9.5) * mm});
            skLineSegment(sketch, "E52.2.0.14", {"start": v(5, 18.5) * mm, "end": v(5, 15.5) * mm});
            skLineSegment(sketch, "E52.2.0.15", {"start": v(134, 42) * mm, "end": v(146, 42) * mm});
            skLineSegment(sketch, "E52.2.0.16", {"start": v(146, 8) * mm, "end": v(134, 8) * mm});
            skLineSegment(sketch, "E52.2.0.17", {"start": v(147.5, 39) * mm, "end": v(147.5, 47) * mm});
            skLineSegment(sketch, "E52.2.0.18", {"start": v(98.5, 2.5) * mm, "end": v(65, 2.5) * mm});
            skLineSegment(sketch, "E52.2.0.19", {"start": v(105, 4.5) * mm, "end": v(105, 1.5) * mm});
            skLineSegment(sketch, "E52.2.0.20", {"start": v(65, 34.5) * mm, "end": v(55, 34.5) * mm});
            skLineSegment(sketch, "E52.2.0.21", {"start": v(84, 42) * mm, "end": v(96, 42) * mm});
            skLineSegment(sketch, "E52.2.0.22", {"start": v(15, 7.5) * mm, "end": v(5, 7.5) * mm});
            skLineSegment(sketch, "E52.2.0.23", {"start": v(65, 31.5) * mm, "end": v(55, 31.5) * mm});
            skLineSegment(sketch, "E52.2.0.24", {"start": v(15, 34.5) * mm, "end": v(5, 34.5) * mm});
            skLineSegment(sketch, "E52.2.0.25", {"start": v(98.5, 39) * mm, "end": v(98.5, 48) * mm});
            skLineSegment(sketch, "E52.2.0.26", {"start": v(147.5, 3.5) * mm, "end": v(147.5, 11) * mm});
            skLineSegment(sketch, "E52.2.0.27", {"start": v(65, 15.5) * mm, "end": v(55, 15.5) * mm});
            skLineSegment(sketch, "E52.2.0.28", {"start": v(34, 24.5) * mm, "end": v(15, 24.5) * mm});
            skLineSegment(sketch, "E52.2.0.29", {"start": v(115, 31.5) * mm, "end": v(105, 31.5) * mm});
            skLineSegment(sketch, "E52.2.0.30", {"start": v(148.5, 39) * mm, "end": v(148.5, 48) * mm});
            skLineSegment(sketch, "E52.2.0.31", {"start": v(34, 40) * mm, "end": v(46, 40) * mm});
            skLineSegment(sketch, "E52.2.0.32", {"start": v(115, 18.5) * mm, "end": v(105, 18.5) * mm});
            skLineSegment(sketch, "E52.2.0.33", {"start": v(84, 41.5) * mm, "end": v(65, 41.5) * mm});
            skLineSegment(sketch, "E52.2.0.34", {"start": v(81, 33.5) * mm, "end": v(81, 39) * mm});
            skLineSegment(sketch, "E52.2.0.35", {"start": v(97.5, 3.5) * mm, "end": v(97.5, 11) * mm});
            skLineSegment(sketch, "E52.2.0.36", {"start": v(146, 26) * mm, "end": v(134, 26) * mm});
            skLineSegment(sketch, "E52.2.0.37", {"start": v(49, 23) * mm, "end": v(49, 11) * mm});
            skLineSegment(sketch, "E52.2.0.38", {"start": v(131, 27) * mm, "end": v(131, 32.5) * mm});
            skLineSegment(sketch, "E52.2.0.39", {"start": v(134, 40) * mm, "end": v(146, 40) * mm});
            skLineSegment(sketch, "E52.2.0.40", {"start": v(55, 4.5) * mm, "end": v(55, 1.5) * mm});
            skLineSegment(sketch, "E52.2.0.41", {"start": v(148.5, 2.5) * mm, "end": v(148.5, 11) * mm});
            skLineSegment(sketch, "E52.2.0.42", {"start": v(97.5, 47) * mm, "end": v(65, 47) * mm});
            skLineSegment(sketch, "E52.2.0.43", {"start": v(46, 26) * mm, "end": v(34, 26) * mm});
            skLineSegment(sketch, "E52.2.0.44", {"start": v(105, 49) * mm, "end": v(115, 49) * mm});
            skLineSegment(sketch, "E52.2.0.45", {"start": v(5, 26.5) * mm, "end": v(5, 23.5) * mm});
            skLineSegment(sketch, "E52.2.0.46", {"start": v(133, 11) * mm, "end": v(133, 23) * mm});
            skLineSegment(sketch, "E52.2.0.47", {"start": v(31, 33.5) * mm, "end": v(15, 33.5) * mm});
            skLineSegment(sketch, "E52.2.0.48", {"start": v(96, 10) * mm, "end": v(84, 10) * mm});
            skLineSegment(sketch, "E52.2.0.49", {"start": v(48.5, 2.5) * mm, "end": v(15, 2.5) * mm});
            skLineSegment(sketch, "E52.2.0.50", {"start": v(105, 18.5) * mm, "end": v(105, 15.5) * mm});
            skLineSegment(sketch, "E52.2.0.51", {"start": v(31, 17.5) * mm, "end": v(15, 17.5) * mm});
            skLineSegment(sketch, "E52.2.0.52", {"start": v(84, 24.5) * mm, "end": v(65, 24.5) * mm});
            skLineSegment(sketch, "E52.2.0.53", {"start": v(96, 26) * mm, "end": v(84, 26) * mm});
            skLineSegment(sketch, "E52.2.0.54", {"start": v(81, 27) * mm, "end": v(81, 32.5) * mm});
            skLineSegment(sketch, "E52.2.0.55", {"start": v(83, 27) * mm, "end": v(83, 39) * mm});
            skLineSegment(sketch, "E52.2.0.56", {"start": v(55, 42.5) * mm, "end": v(55, 39.5) * mm});
            skLineSegment(sketch, "E52.2.0.57", {"start": v(115, 46) * mm, "end": v(105, 46) * mm});
            skLineSegment(sketch, "E52.2.0.58", {"start": v(15, 15.5) * mm, "end": v(5, 15.5) * mm});
            skLineSegment(sketch, "E52.2.0.59", {"start": v(65, 46) * mm, "end": v(55, 46) * mm});
            skLineSegment(sketch, "E52.2.0.60", {"start": v(147, 23) * mm, "end": v(147, 11) * mm});
            skLineSegment(sketch, "E52.2.0.61", {"start": v(65, 7.5) * mm, "end": v(55, 7.5) * mm});
            skLineSegment(sketch, "E52.2.0.62", {"start": v(47.5, 3.5) * mm, "end": v(15, 3.5) * mm});
            skLineSegment(sketch, "E52.2.0.63", {"start": v(146, 24) * mm, "end": v(134, 24) * mm});
            skLineSegment(sketch, "E52.2.0.64", {"start": v(134, 9.5) * mm, "end": v(115, 9.5) * mm});
            skLineSegment(sketch, "E52.2.0.65", {"start": v(133, 27) * mm, "end": v(133, 39) * mm});
            skLineSegment(sketch, "E52.2.0.66", {"start": v(98.5, 48) * mm, "end": v(65, 48) * mm});
            skLineSegment(sketch, "E52.2.0.67", {"start": v(31, 32.5) * mm, "end": v(15, 32.5) * mm});
            skLineSegment(sketch, "E52.2.0.68", {"start": v(49, 39) * mm, "end": v(49, 27) * mm});
            skLineSegment(sketch, "E52.2.0.69", {"start": v(131, 11) * mm, "end": v(131, 16.5) * mm});
            skLineSegment(sketch, "E52.2.0.70", {"start": v(31, 16.5) * mm, "end": v(15, 16.5) * mm});
            skLineSegment(sketch, "E52.2.0.71", {"start": v(5, 39.5) * mm, "end": v(15, 39.5) * mm});
            skLineSegment(sketch, "E52.2.0.72", {"start": v(55, 49) * mm, "end": v(65, 49) * mm});
            skLineSegment(sketch, "E52.2.0.73", {"start": v(81, 17.5) * mm, "end": v(81, 23) * mm});
            skLineSegment(sketch, "E52.2.0.74", {"start": v(65, 26.5) * mm, "end": v(55, 26.5) * mm});
            skLineSegment(sketch, "E52.2.0.75", {"start": v(115, 23.5) * mm, "end": v(105, 23.5) * mm});
            skLineSegment(sketch, "E52.2.0.76", {"start": v(115, 34.5) * mm, "end": v(105, 34.5) * mm});
            skLineSegment(sketch, "E52.2.0.77", {"start": v(5, 34.5) * mm, "end": v(5, 31.5) * mm});
            skLineSegment(sketch, "E52.2.0.78", {"start": v(115, 26.5) * mm, "end": v(105, 26.5) * mm});
            skLineSegment(sketch, "E52.2.0.79", {"start": v(47.5, 39) * mm, "end": v(47.5, 47) * mm});
            skLineSegment(sketch, "E52.2.0.80", {"start": v(148.5, 2.5) * mm, "end": v(115, 2.5) * mm});
            skLineSegment(sketch, "E52.2.0.81", {"start": v(134, 40.5) * mm, "end": v(115, 40.5) * mm});
            skLineSegment(sketch, "E52.2.0.82", {"start": v(105, 39.5) * mm, "end": v(115, 39.5) * mm});
            skLineSegment(sketch, "E52.2.0.83", {"start": v(65, 10.5) * mm, "end": v(55, 10.5) * mm});
            skLineSegment(sketch, "E52.2.0.84", {"start": v(33, 27) * mm, "end": v(33, 39) * mm});
            skLineSegment(sketch, "E52.2.0.85", {"start": v(97, 23) * mm, "end": v(97, 11) * mm});
            skLineSegment(sketch, "E52.2.0.86", {"start": v(147.5, 47) * mm, "end": v(115, 47) * mm});
            skLineSegment(sketch, "E52.2.0.87", {"start": v(105, 26.5) * mm, "end": v(105, 23.5) * mm});
            skLineSegment(sketch, "E52.2.0.88", {"start": v(97, 39) * mm, "end": v(97, 27) * mm});
            skLineSegment(sketch, "E52.2.0.89", {"start": v(34, 42) * mm, "end": v(46, 42) * mm});
            skLineSegment(sketch, "E52.2.0.90", {"start": v(149, 39) * mm, "end": v(149, 27) * mm});
            skLineSegment(sketch, "E52.2.0.91", {"start": v(147, 39) * mm, "end": v(147, 27) * mm});
            skLineSegment(sketch, "E52.2.0.92", {"start": v(34, 40.5) * mm, "end": v(15, 40.5) * mm});
            skLineSegment(sketch, "E52.2.0.93", {"start": v(97.5, 3.5) * mm, "end": v(65, 3.5) * mm});
            skLineSegment(sketch, "E52.2.0.94", {"start": v(5, 10.5) * mm, "end": v(5, 7.5) * mm});
            skLineSegment(sketch, "E52.2.0.95", {"start": v(5, 49) * mm, "end": v(15, 49) * mm});
            skLineSegment(sketch, "E52.2.0.96", {"start": v(134, 24.5) * mm, "end": v(115, 24.5) * mm});
            skLineSegment(sketch, "E52.2.0.97", {"start": v(81, 33.5) * mm, "end": v(65, 33.5) * mm});
            skLineSegment(sketch, "E52.2.0.98", {"start": v(134, 8.5) * mm, "end": v(115, 8.5) * mm});
            skLineSegment(sketch, "E52.2.0.99", {"start": v(65, 18.5) * mm, "end": v(55, 18.5) * mm});
            skLineSegment(sketch, "E52.2.0.100", {"start": v(34, 8.5) * mm, "end": v(15, 8.5) * mm});
            skLineSegment(sketch, "E52.2.0.101", {"start": v(15, 46) * mm, "end": v(5, 46) * mm});
            skLineSegment(sketch, "E52.2.0.102", {"start": v(47, 39) * mm, "end": v(47, 27) * mm});
            skLineSegment(sketch, "E52.2.0.103", {"start": v(15, 23.5) * mm, "end": v(5, 23.5) * mm});
            skLineSegment(sketch, "E52.2.0.104", {"start": v(115, 7.5) * mm, "end": v(105, 7.5) * mm});
            skLineSegment(sketch, "E52.2.0.105", {"start": v(5, 46) * mm, "end": v(5, 49) * mm});
            skLineSegment(sketch, "E52.2.0.106", {"start": v(55, 10.5) * mm, "end": v(55, 7.5) * mm});
            skLineSegment(sketch, "E52.2.0.107", {"start": v(46, 24) * mm, "end": v(34, 24) * mm});
            skLineSegment(sketch, "E52.2.0.108", {"start": v(48.5, 48) * mm, "end": v(15, 48) * mm});
            skLineSegment(sketch, "E52.2.0.109", {"start": v(31, 17.5) * mm, "end": v(31, 23) * mm});
            skLineSegment(sketch, "E52.2.0.110", {"start": v(15, 18.5) * mm, "end": v(5, 18.5) * mm});
            skLineSegment(sketch, "E52.2.0.111", {"start": v(47, 23) * mm, "end": v(47, 11) * mm});
            skLineSegment(sketch, "E52.2.0.112", {"start": v(131, 17.5) * mm, "end": v(131, 23) * mm});
            skLineSegment(sketch, "E52.2.0.113", {"start": v(84, 8.5) * mm, "end": v(65, 8.5) * mm});
            skLineSegment(sketch, "E52.2.0.114", {"start": v(46, 8) * mm, "end": v(34, 8) * mm});
            skLineSegment(sketch, "E52.2.0.115", {"start": v(149, 23) * mm, "end": v(149, 11) * mm});
            skLineSegment(sketch, "E52.2.0.116", {"start": v(115, 42.5) * mm, "end": v(105, 42.5) * mm});
            skLineSegment(sketch, "E52.2.0.117", {"start": v(65, 4.5) * mm, "end": v(55, 4.5) * mm});
            skLineSegment(sketch, "E52.2.0.118", {"start": v(131, 33.5) * mm, "end": v(115, 33.5) * mm});
            skLineSegment(sketch, "E52.2.0.119", {"start": v(83, 11) * mm, "end": v(83, 23) * mm});
            skLineSegment(sketch, "E52.2.0.120", {"start": v(55, 39.5) * mm, "end": v(65, 39.5) * mm});
            skLineSegment(sketch, "E52.2.0.121", {"start": v(131, 16.5) * mm, "end": v(115, 16.5) * mm});
            skLineSegment(sketch, "E52.2.0.122", {"start": v(84, 40.5) * mm, "end": v(65, 40.5) * mm});
            skLineSegment(sketch, "E52.2.0.123", {"start": v(131, 17.5) * mm, "end": v(115, 17.5) * mm});
            skLineSegment(sketch, "E52.2.0.124", {"start": v(131, 32.5) * mm, "end": v(115, 32.5) * mm});
            skLineSegment(sketch, "E52.2.0.125", {"start": v(55, 34.5) * mm, "end": v(55, 31.5) * mm});
            skLineSegment(sketch, "E52.2.0.126", {"start": v(115, 15.5) * mm, "end": v(105, 15.5) * mm});
            skLineSegment(sketch, "E52.2.0.127", {"start": v(15, 10.5) * mm, "end": v(5, 10.5) * mm});
            skLineSegment(sketch, "E52.2.0.128", {"start": v(105, 42.5) * mm, "end": v(105, 39.5) * mm});
            skLineSegment(sketch, "E52.2.0.129", {"start": v(134, 41.5) * mm, "end": v(115, 41.5) * mm});
            skLineSegment(sketch, "E52.2.0.130", {"start": v(46, 10) * mm, "end": v(34, 10) * mm});
            skLineSegment(sketch, "E52.2.0.131", {"start": v(31, 11) * mm, "end": v(31, 16.5) * mm});
            skLineSegment(sketch, "E52.2.0.132", {"start": v(15, 31.5) * mm, "end": v(5, 31.5) * mm});
            skLineSegment(sketch, "E52.2.0.133", {"start": v(105, 46) * mm, "end": v(105, 49) * mm});
            skLineSegment(sketch, "E52.2.0.134", {"start": v(115, 4.5) * mm, "end": v(105, 4.5) * mm});
            skLineSegment(sketch, "E52.2.0.135", {"start": v(81, 16.5) * mm, "end": v(65, 16.5) * mm});
            skLineSegment(sketch, "E52.2.0.136", {"start": v(81, 32.5) * mm, "end": v(65, 32.5) * mm});
            skLineSegment(sketch, "E52.2.0.137", {"start": v(65, 42.5) * mm, "end": v(55, 42.5) * mm});
            skLineSegment(sketch, "E52.2.0.138", {"start": v(48.5, 39) * mm, "end": v(48.5, 48) * mm});
            skLineSegment(sketch, "E52.2.0.139", {"start": v(81, 11) * mm, "end": v(81, 16.5) * mm});
            skLineSegment(sketch, "E52.2.0.140", {"start": v(97.5, 39) * mm, "end": v(97.5, 47) * mm});
            skLineSegment(sketch, "E52.2.0.141", {"start": v(84, 40) * mm, "end": v(96, 40) * mm});
            skLineSegment(sketch, "E52.2.0.142", {"start": v(98.5, 2.5) * mm, "end": v(98.5, 11) * mm});
            skLineSegment(sketch, "E52.2.0.143", {"start": v(47.5, 47) * mm, "end": v(15, 47) * mm});
            skLineSegment(sketch, "E52.2.0.144", {"start": v(96, 24) * mm, "end": v(84, 24) * mm});
            skLineSegment(sketch, "E52.2.0.145", {"start": v(148.5, 48) * mm, "end": v(115, 48) * mm});
            skLineSegment(sketch, "E52.2.0.146", {"start": v(33, 11) * mm, "end": v(33, 23) * mm});
            skLineSegment(sketch, "E52.2.0.147", {"start": v(55, 46) * mm, "end": v(55, 49) * mm});
            skLineSegment(sketch, "E52.2.0.148", {"start": v(34, 9.5) * mm, "end": v(15, 9.5) * mm});
            skLineSegment(sketch, "E52.2.0.149", {"start": v(31, 27) * mm, "end": v(31, 32.5) * mm});
            skLineSegment(sketch, "E52.2.0.150", {"start": v(34, 41.5) * mm, "end": v(15, 41.5) * mm});
            skLineSegment(sketch, "E52.2.0.151", {"start": v(34, 25.5) * mm, "end": v(15, 25.5) * mm});
            skLineSegment(sketch, "E52.2.0.152", {"start": v(47.5, 3.5) * mm, "end": v(47.5, 11) * mm});
            skLineSegment(sketch, "E52.2.0.153", {"start": v(105, 10.5) * mm, "end": v(105, 7.5) * mm});
            skLineSegment(sketch, "E52.2.0.154", {"start": v(65, 1.5) * mm, "end": v(55, 1.5) * mm});
            skLineSegment(sketch, "E52.2.0.155", {"start": v(65, 23.5) * mm, "end": v(55, 23.5) * mm});
            skLineSegment(sketch, "E52.2.0.156", {"start": v(55, 18.5) * mm, "end": v(55, 15.5) * mm});
            skLineSegment(sketch, "E52.2.0.157", {"start": v(48.5, 2.5) * mm, "end": v(48.5, 11) * mm});
            skLineSegment(sketch, "E52.2.0.158", {"start": v(115, 10.5) * mm, "end": v(105, 10.5) * mm});
            skLineSegment(sketch, "E52.2.0.159", {"start": v(146, 10) * mm, "end": v(134, 10) * mm});
            skLineSegment(sketch, "E52.2.0.160", {"start": v(131, 33.5) * mm, "end": v(131, 39) * mm});
            skLineSegment(sketch, "E52.2.0.161", {"start": v(147.5, 3.5) * mm, "end": v(115, 3.5) * mm});
            skLineSegment(sketch, "E52.2.0.162", {"start": v(15, 42.5) * mm, "end": v(5, 42.5) * mm});
            skLineSegment(sketch, "E52.2.0.163", {"start": v(15, 1.5) * mm, "end": v(5, 1.5) * mm});
            skLineSegment(sketch, "E52.2.0.164", {"start": v(55, 26.5) * mm, "end": v(55, 23.5) * mm});
            skLineSegment(sketch, "E52.2.0.165", {"start": v(31, 33.5) * mm, "end": v(31, 39) * mm});
            skLineSegment(sketch, "E52.2.0.166", {"start": v(84, 42) * mm, "end": v(84, 41.5) * mm});
            skLineSegment(sketch, "E52.2.0.167", {"start": v(84, 8.5) * mm, "end": v(84, 8) * mm});
            skLineSegment(sketch, "E52.2.0.168", {"start": v(46, 26) * mm, "end": v(46, 24) * mm});
            skLineSegment(sketch, "E52.2.0.169", {"start": v(34, 42) * mm, "end": v(34, 41.5) * mm});
            skLineSegment(sketch, "E52.2.0.170", {"start": v(15, 4.5) * mm, "end": v(15, 3.5) * mm});
            skLineSegment(sketch, "E52.2.0.171", {"start": v(115, 47) * mm, "end": v(115, 46) * mm});
            skLineSegment(sketch, "E52.2.0.172", {"start": v(115, 34.5) * mm, "end": v(115, 33.5) * mm});
            skLineSegment(sketch, "E52.2.0.173", {"start": v(146, 10) * mm, "end": v(146, 8) * mm});
            skLineSegment(sketch, "E52.2.0.174", {"start": v(15, 18.5) * mm, "end": v(15, 17.5) * mm});
            skLineSegment(sketch, "E52.2.0.175", {"start": v(15, 34.5) * mm, "end": v(15, 33.5) * mm});
            skLineSegment(sketch, "E52.2.0.176", {"start": v(133, 27) * mm, "end": v(131, 27) * mm});
            skLineSegment(sketch, "E52.2.0.177", {"start": v(134, 8.5) * mm, "end": v(134, 8) * mm});
            skLineSegment(sketch, "E52.2.0.178", {"start": v(133, 11) * mm, "end": v(131, 11) * mm});
            skLineSegment(sketch, "E52.2.0.179", {"start": v(34, 10) * mm, "end": v(34, 9.5) * mm});
            skLineSegment(sketch, "E52.2.0.180", {"start": v(146, 26) * mm, "end": v(146, 24) * mm});
            skLineSegment(sketch, "E52.2.0.181", {"start": v(83, 39) * mm, "end": v(81, 39) * mm});
            skLineSegment(sketch, "E52.2.0.182", {"start": v(97, 39) * mm, "end": v(99, 39) * mm});
            skLineSegment(sketch, "E52.2.0.183", {"start": v(47, 27) * mm, "end": v(49, 27) * mm});
            skLineSegment(sketch, "E52.2.0.184", {"start": v(146, 42) * mm, "end": v(146, 40) * mm});
            skLineSegment(sketch, "E52.2.0.185", {"start": v(15, 16.5) * mm, "end": v(15, 15.5) * mm});
            skLineSegment(sketch, "E52.2.0.186", {"start": v(33, 27) * mm, "end": v(31, 27) * mm});
            skLineSegment(sketch, "E52.2.0.187", {"start": v(47, 23) * mm, "end": v(49, 23) * mm});
            skLineSegment(sketch, "E52.2.0.188", {"start": v(65, 47) * mm, "end": v(65, 46) * mm});
            skLineSegment(sketch, "E52.2.0.189", {"start": v(134, 10) * mm, "end": v(134, 9.5) * mm});
            skLineSegment(sketch, "E52.2.0.190", {"start": v(65, 4.5) * mm, "end": v(65, 3.5) * mm});
            skLineSegment(sketch, "E52.2.0.191", {"start": v(97, 27) * mm, "end": v(99, 27) * mm});
            skLineSegment(sketch, "E52.2.0.192", {"start": v(147, 39) * mm, "end": v(149, 39) * mm});
            skLineSegment(sketch, "E52.2.0.193", {"start": v(65, 18.5) * mm, "end": v(65, 17.5) * mm});
            skLineSegment(sketch, "E52.2.0.194", {"start": v(33, 39) * mm, "end": v(31, 39) * mm});
            skLineSegment(sketch, "E52.2.0.195", {"start": v(147, 27) * mm, "end": v(149, 27) * mm});
            skLineSegment(sketch, "E52.2.0.196", {"start": v(133, 39) * mm, "end": v(131, 39) * mm});
            skLineSegment(sketch, "E52.2.0.197", {"start": v(98.5, 11) * mm, "end": v(99, 11) * mm});
            skLineSegment(sketch, "E52.2.0.198", {"start": v(46, 10) * mm, "end": v(46, 8) * mm});
            skLineSegment(sketch, "E52.2.0.199", {"start": v(83, 27) * mm, "end": v(81, 27) * mm});
            skLineSegment(sketch, "E52.2.0.200", {"start": v(84, 24.5) * mm, "end": v(84, 24) * mm});
            skLineSegment(sketch, "E52.2.0.201", {"start": v(96, 10) * mm, "end": v(96, 8) * mm});
            skLineSegment(sketch, "E52.2.0.202", {"start": v(46, 42) * mm, "end": v(46, 40) * mm});
            skLineSegment(sketch, "E52.2.0.203", {"start": v(133, 23) * mm, "end": v(131, 23) * mm});
            skLineSegment(sketch, "E52.2.0.204", {"start": v(47, 11) * mm, "end": v(47.5, 11) * mm});
            skLineSegment(sketch, "E52.2.0.205", {"start": v(147, 23) * mm, "end": v(149, 23) * mm});
            skLineSegment(sketch, "E52.2.0.206", {"start": v(83, 11) * mm, "end": v(81, 11) * mm});
            skLineSegment(sketch, "E52.2.0.207", {"start": v(115, 4.5) * mm, "end": v(115, 3.5) * mm});
            skLineSegment(sketch, "E52.2.0.208", {"start": v(147, 11) * mm, "end": v(147.5, 11) * mm});
            skLineSegment(sketch, "E52.2.0.209", {"start": v(96, 42) * mm, "end": v(96, 40) * mm});
            skLineSegment(sketch, "E52.2.0.210", {"start": v(115, 26.5) * mm, "end": v(115, 25.5) * mm});
            skLineSegment(sketch, "E52.2.0.211", {"start": v(15, 41.5) * mm, "end": v(15, 42.5) * mm});
            skLineSegment(sketch, "E52.2.0.212", {"start": v(97, 11) * mm, "end": v(97.5, 11) * mm});
            skLineSegment(sketch, "E52.2.0.213", {"start": v(83, 23) * mm, "end": v(81, 23) * mm});
            skLineSegment(sketch, "E52.2.0.214", {"start": v(97, 23) * mm, "end": v(99, 23) * mm});
            skLineSegment(sketch, "E52.2.0.215", {"start": v(15, 10.5) * mm, "end": v(15, 9.5) * mm});
            skLineSegment(sketch, "E52.2.0.216", {"start": v(15, 26.5) * mm, "end": v(15, 25.5) * mm});
            skLineSegment(sketch, "E52.2.0.217", {"start": v(115, 18.5) * mm, "end": v(115, 17.5) * mm});
            skLineSegment(sketch, "E52.2.0.218", {"start": v(33, 23) * mm, "end": v(31, 23) * mm});
            skLineSegment(sketch, "E52.2.0.219", {"start": v(33, 11) * mm, "end": v(31, 11) * mm});
            skLineSegment(sketch, "E52.2.0.220", {"start": v(134, 26) * mm, "end": v(134, 25.5) * mm});
            skLineSegment(sketch, "E52.2.0.221", {"start": v(96, 26) * mm, "end": v(96, 24) * mm});
            skLineSegment(sketch, "E52.2.0.222", {"start": v(148.5, 11) * mm, "end": v(149, 11) * mm});
            skLineSegment(sketch, "E52.2.0.223", {"start": v(34, 8.5) * mm, "end": v(34, 8) * mm});
            skLineSegment(sketch, "E52.2.0.224", {"start": v(15, 8.5) * mm, "end": v(15, 7.5) * mm});
            skLineSegment(sketch, "E52.2.0.225", {"start": v(84, 26) * mm, "end": v(84, 25.5) * mm});
            skLineSegment(sketch, "E52.2.0.226", {"start": v(15, 32.5) * mm, "end": v(15, 31.5) * mm});
            skLineSegment(sketch, "E52.2.0.227", {"start": v(34, 26) * mm, "end": v(34, 25.5) * mm});
            skLineSegment(sketch, "E52.2.0.228", {"start": v(134, 24.5) * mm, "end": v(134, 24) * mm});
            skLineSegment(sketch, "E52.2.0.229", {"start": v(15, 2.5) * mm, "end": v(15, 1.5) * mm});
            skLineSegment(sketch, "E52.2.0.230", {"start": v(48.5, 11) * mm, "end": v(49, 11) * mm});
            skLineSegment(sketch, "E52.2.0.231", {"start": v(115, 41.5) * mm, "end": v(115, 42.5) * mm});
            skLineSegment(sketch, "E52.2.0.232", {"start": v(115, 39.5) * mm, "end": v(115, 40.5) * mm});
            skLineSegment(sketch, "E52.2.0.233", {"start": v(65, 32.5) * mm, "end": v(65, 31.5) * mm});
            skLineSegment(sketch, "E52.2.0.234", {"start": v(65, 8.5) * mm, "end": v(65, 7.5) * mm});
            skLineSegment(sketch, "E52.2.0.235", {"start": v(47, 39) * mm, "end": v(49, 39) * mm});
            skLineSegment(sketch, "E52.2.0.236", {"start": v(34, 24.5) * mm, "end": v(34, 24) * mm});
            skLineSegment(sketch, "E52.2.0.237", {"start": v(115, 49) * mm, "end": v(115, 48) * mm});
            skLineSegment(sketch, "E52.2.0.238", {"start": v(134, 40.5) * mm, "end": v(134, 40) * mm});
            skLineSegment(sketch, "E52.2.0.239", {"start": v(65, 41.5) * mm, "end": v(65, 42.5) * mm});
            skLineSegment(sketch, "E52.2.0.240", {"start": v(65, 26.5) * mm, "end": v(65, 25.5) * mm});
            skLineSegment(sketch, "E52.2.0.241", {"start": v(84, 10) * mm, "end": v(84, 9.5) * mm});
            skLineSegment(sketch, "E52.2.0.242", {"start": v(115, 24.5) * mm, "end": v(115, 23.5) * mm});
            skLineSegment(sketch, "E52.2.0.243", {"start": v(65, 2.5) * mm, "end": v(65, 1.5) * mm});
            skLineSegment(sketch, "E52.2.0.244", {"start": v(65, 49) * mm, "end": v(65, 48) * mm});
            skLineSegment(sketch, "E52.2.0.245", {"start": v(115, 8.5) * mm, "end": v(115, 7.5) * mm});
            skLineSegment(sketch, "E52.2.0.246", {"start": v(115, 10.5) * mm, "end": v(115, 9.5) * mm});
            skLineSegment(sketch, "E52.2.0.247", {"start": v(65, 16.5) * mm, "end": v(65, 15.5) * mm});
            skLineSegment(sketch, "E52.2.0.248", {"start": v(84, 40.5) * mm, "end": v(84, 40) * mm});
            skLineSegment(sketch, "E52.2.0.249", {"start": v(65, 10.5) * mm, "end": v(65, 9.5) * mm});
            skLineSegment(sketch, "E52.2.0.250", {"start": v(15, 39.5) * mm, "end": v(15, 40.5) * mm});
            skLineSegment(sketch, "E52.2.0.251", {"start": v(15, 24.5) * mm, "end": v(15, 23.5) * mm});
            skLineSegment(sketch, "E52.2.0.252", {"start": v(65, 39.5) * mm, "end": v(65, 40.5) * mm});
            skLineSegment(sketch, "E52.2.0.253", {"start": v(65, 34.5) * mm, "end": v(65, 33.5) * mm});
            skLineSegment(sketch, "E52.2.0.254", {"start": v(15, 49) * mm, "end": v(15, 48) * mm});
            skLineSegment(sketch, "E52.2.0.255", {"start": v(65, 24.5) * mm, "end": v(65, 23.5) * mm});
            skLineSegment(sketch, "E52.2.0.256", {"start": v(134, 42) * mm, "end": v(134, 41.5) * mm});
            skLineSegment(sketch, "E52.2.0.257", {"start": v(115, 2.5) * mm, "end": v(115, 1.5) * mm});
            skLineSegment(sketch, "E52.2.0.258", {"start": v(115, 16.5) * mm, "end": v(115, 15.5) * mm});
            skLineSegment(sketch, "E52.2.0.259", {"start": v(115, 32.5) * mm, "end": v(115, 31.5) * mm});
            skLineSegment(sketch, "E52.2.0.260", {"start": v(15, 47) * mm, "end": v(15, 46) * mm});
            skLineSegment(sketch, "E52.2.0.261", {"start": v(34, 40.5) * mm, "end": v(34, 40) * mm});
            skLineSegment(sketch, "E52.direction1", {"start": v(5, 101.5) * mm, "end": v(5, 51.5) * mm, "construction": true});
            skSolve(sketch);
        }
        {
            var Q0;
            Q0 = qSketchRegion(id + "F3", true);
            extrude(context, id + "F4", {"entities" : qUnion([Q0]), "operationType" : NewBodyOperationType.REMOVE, "endBound" : BoundingType.THROUGH_ALL, "oppositeDirection" : true, "depth" : 25 * mm, "offsetDistance" : 25 * mm});
        }
    });
